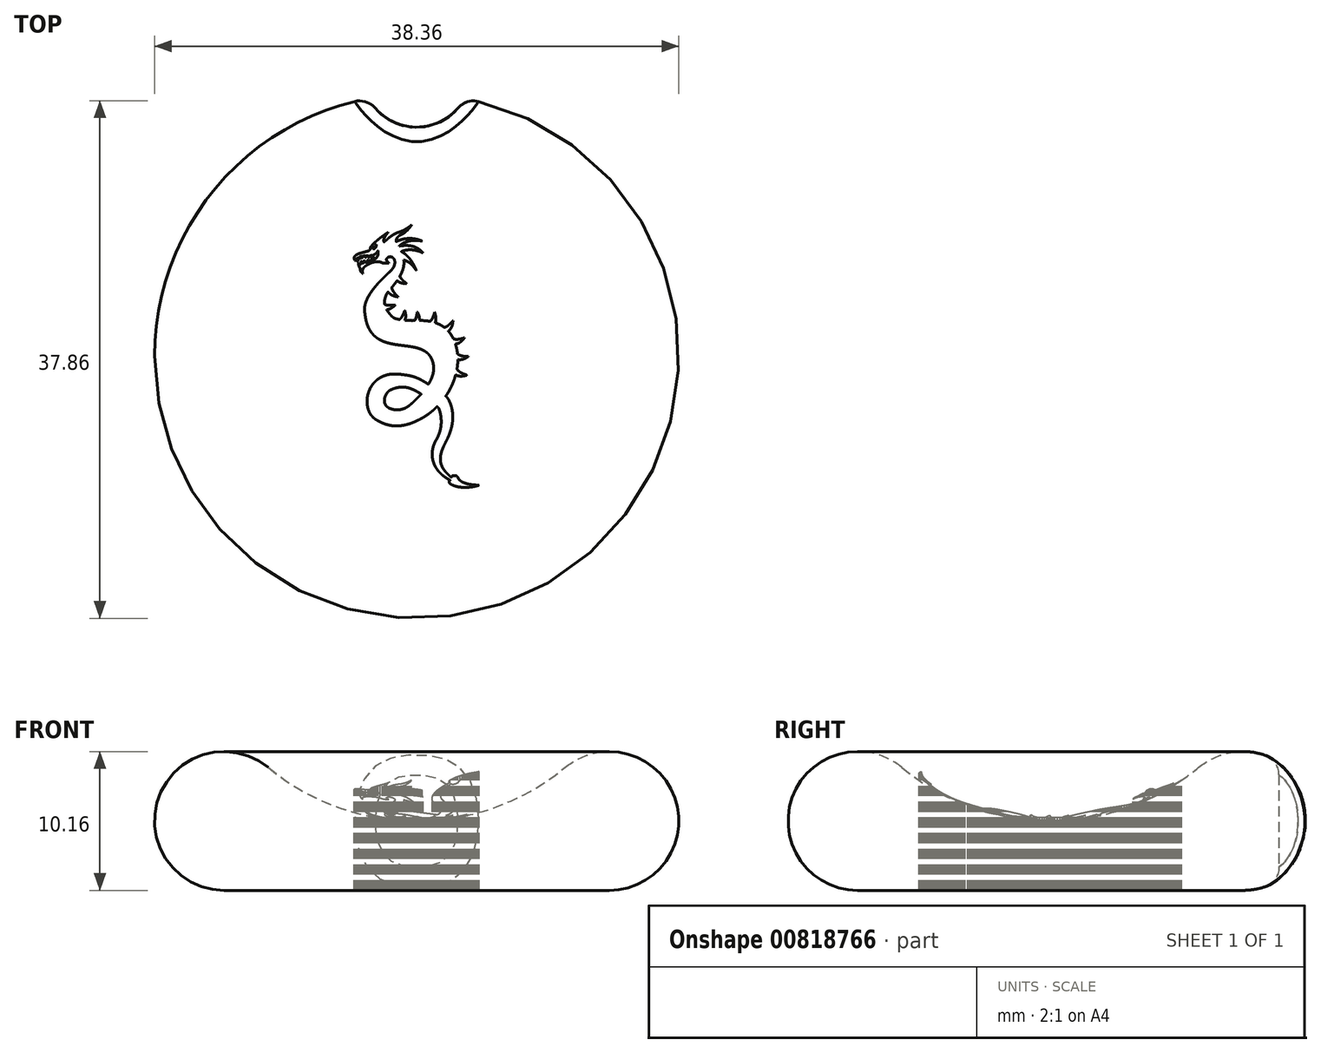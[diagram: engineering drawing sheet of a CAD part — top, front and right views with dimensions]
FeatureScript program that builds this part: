
annotation { "Feature Type Name" : "Feature", "Feature Type Description" : "" }
export const myFeature = defineFeature(function(context is Context, id is Id, definition is map)
    precondition{}
    {
        {
            var Q0;
            Q0=qCreatedBy(makeId("Front.planeOp"),FACE);
            var sketch = newSketch(context, id + "F0", { "sketchPlane" : qUnion([Q0])});
            skArc(sketch, "E0", {"start": v(-10.86, 9) * mm, "mid": v(-18.88, 6.8) * mm, "end": v(-14.1, 0) * mm});
            skArc(sketch, "E1", {"start": v(-10.86, 9) * mm, "mid": v(-5.77, 6.09) * mm, "end": v(0, 5.08) * mm});
            skLineSegment(sketch, "E2", {"start": v(-14.1, 0) * mm, "end": v(0, 0) * mm});
            skLineSegment(sketch, "E3", {"start": v(0, 0) * mm, "end": v(0, 5.08) * mm});
            skPoint(sketch, "E4.orphan", {"position": v(-9.13, 0) * mm});
            skSolve(sketch);
        }
        {
            var Q0;
            Q0=makeQuery(id+"F0.imprint","IMPRINT",FACE,{"disambiguationData":[TD([[makeQuery(id+"F0.imprint","IMPRINT",EDGE,{"derivedFrom":sQuery(id+"F0.wireOp",EDGE,"E0")}),1.0]])]});
            var Q1;
            Q1=sQuery(id+"F0.wireOp",EDGE,"E3");
            revolve(context, id + "F1", {"surfaceOperationType" : NewSurfaceOperationType.NEW, "entities" : qUnion([Q0]), "axis" : qUnion([Q1]), "revolveType" : RevolveType.FULL});
        }
        {
            var Q0;
            Q0=qCreatedBy(makeId("Top.planeOp"),FACE);
            cPlane(context, id + "F2", {"entities" : qUnion([Q0]), "cplaneType" : CPlaneType.OFFSET, "offset" : 10.16 * mm, "width" : 152.4 * mm, "height" : 152.4 * mm});
        }
        {
            var Q0;
            Q0=qCreatedBy(id+"F2.planeOp",FACE);
            var sketch = newSketch(context, id + "F3", { "sketchPlane" : qUnion([Q0])});
            skLineSegment(sketch, "E5", {"start": v(-2.95, 8.17) * mm, "end": v(-2.96, 8.11) * mm});
            skLineSegment(sketch, "E6", {"start": v(-2.96, 8.11) * mm, "end": v(-2.97, 8.05) * mm});
            skLineSegment(sketch, "E7", {"start": v(-2.97, 8.05) * mm, "end": v(-2.98, 8) * mm});
            skLineSegment(sketch, "E8", {"start": v(-2.98, 8) * mm, "end": v(-3, 7.95) * mm});
            skLineSegment(sketch, "E9", {"start": v(-3, 7.95) * mm, "end": v(-3.03, 7.91) * mm});
            skLineSegment(sketch, "E10", {"start": v(-3.03, 7.91) * mm, "end": v(-3.06, 7.88) * mm});
            skLineSegment(sketch, "E11", {"start": v(-3.06, 7.88) * mm, "end": v(-3.09, 7.86) * mm});
            skLineSegment(sketch, "E12", {"start": v(-3.09, 7.86) * mm, "end": v(-3.12, 7.85) * mm});
            skLineSegment(sketch, "E13", {"start": v(-3.12, 7.85) * mm, "end": v(-3.14, 7.85) * mm});
            skLineSegment(sketch, "E14", {"start": v(-3.14, 7.85) * mm, "end": v(-3.16, 7.85) * mm});
            skLineSegment(sketch, "E15", {"start": v(-3.16, 7.85) * mm, "end": v(-3.18, 7.86) * mm});
            skLineSegment(sketch, "E16", {"start": v(-3.18, 7.86) * mm, "end": v(-3.2, 7.88) * mm});
            skLineSegment(sketch, "E17", {"start": v(-3.2, 7.88) * mm, "end": v(-3.2, 7.9) * mm});
            skLineSegment(sketch, "E18", {"start": v(-3.2, 7.9) * mm, "end": v(-3.2, 7.91) * mm});
            skLineSegment(sketch, "E19", {"start": v(-3.2, 7.91) * mm, "end": v(-3.2, 7.93) * mm});
            skLineSegment(sketch, "E20", {"start": v(-3.2, 7.93) * mm, "end": v(-3.17, 7.95) * mm});
            skLineSegment(sketch, "E21", {"start": v(-3.17, 7.95) * mm, "end": v(-3.12, 7.98) * mm});
            skLineSegment(sketch, "E22", {"start": v(-3.12, 7.98) * mm, "end": v(-3.09, 8) * mm});
            skLineSegment(sketch, "E23", {"start": v(-3.09, 8) * mm, "end": v(-3.06, 8.02) * mm});
            skLineSegment(sketch, "E24", {"start": v(-3.06, 8.02) * mm, "end": v(-3.03, 8.05) * mm});
            skLineSegment(sketch, "E25", {"start": v(-3.03, 8.05) * mm, "end": v(-3, 8.09) * mm});
            skLineSegment(sketch, "E26", {"start": v(-3, 8.09) * mm, "end": v(-2.97, 8.13) * mm});
            skLineSegment(sketch, "E27", {"start": v(-2.97, 8.13) * mm, "end": v(-2.95, 8.17) * mm});
            skLineSegment(sketch, "E28", {"start": v(-1.09, -2.26) * mm, "end": v(-1.02, -2.26) * mm});
            skLineSegment(sketch, "E29", {"start": v(-1.02, -2.26) * mm, "end": v(-0.94, -2.26) * mm});
            skLineSegment(sketch, "E30", {"start": v(-0.94, -2.26) * mm, "end": v(-0.87, -2.27) * mm});
            skLineSegment(sketch, "E31", {"start": v(-0.87, -2.27) * mm, "end": v(-0.8, -2.28) * mm});
            skLineSegment(sketch, "E32", {"start": v(-0.8, -2.28) * mm, "end": v(-0.73, -2.3) * mm});
            skLineSegment(sketch, "E33", {"start": v(-0.73, -2.3) * mm, "end": v(-0.66, -2.3) * mm});
            skLineSegment(sketch, "E34", {"start": v(-0.66, -2.3) * mm, "end": v(-0.52, -2.35) * mm});
            skLineSegment(sketch, "E35", {"start": v(-0.52, -2.35) * mm, "end": v(-0.4, -2.4) * mm});
            skLineSegment(sketch, "E36", {"start": v(-0.4, -2.4) * mm, "end": v(-0.26, -2.45) * mm});
            skLineSegment(sketch, "E37", {"start": v(-0.26, -2.45) * mm, "end": v(-0.13, -2.51) * mm});
            skLineSegment(sketch, "E38", {"start": v(-0.13, -2.51) * mm, "end": v(0, -2.58) * mm});
            skLineSegment(sketch, "E39", {"start": v(0, -2.58) * mm, "end": v(0.17, -2.68) * mm});
            skLineSegment(sketch, "E40", {"start": v(0.17, -2.68) * mm, "end": v(0.34, -2.78) * mm});
            skLineSegment(sketch, "E41", {"start": v(0.34, -2.78) * mm, "end": v(0.25, -2.87) * mm});
            skLineSegment(sketch, "E42", {"start": v(0.25, -2.87) * mm, "end": v(0.17, -2.96) * mm});
            skLineSegment(sketch, "E43", {"start": v(0.17, -2.96) * mm, "end": v(0, -3.12) * mm});
            skLineSegment(sketch, "E44", {"start": v(0, -3.12) * mm, "end": v(-0.17, -3.28) * mm});
            skLineSegment(sketch, "E45", {"start": v(-0.17, -3.28) * mm, "end": v(-0.31, -3.42) * mm});
            skLineSegment(sketch, "E46", {"start": v(-0.31, -3.42) * mm, "end": v(-0.4, -3.5) * mm});
            skLineSegment(sketch, "E47", {"start": v(-0.4, -3.5) * mm, "end": v(-0.49, -3.57) * mm});
            skLineSegment(sketch, "E48", {"start": v(-0.49, -3.57) * mm, "end": v(-0.57, -3.64) * mm});
            skLineSegment(sketch, "E49", {"start": v(-0.57, -3.64) * mm, "end": v(-0.66, -3.7) * mm});
            skLineSegment(sketch, "E50", {"start": v(-0.66, -3.7) * mm, "end": v(-0.74, -3.75) * mm});
            skLineSegment(sketch, "E51", {"start": v(-0.74, -3.75) * mm, "end": v(-0.83, -3.8) * mm});
            skLineSegment(sketch, "E52", {"start": v(-0.83, -3.8) * mm, "end": v(-0.91, -3.83) * mm});
            skLineSegment(sketch, "E53", {"start": v(-0.91, -3.83) * mm, "end": v(-1, -3.86) * mm});
            skLineSegment(sketch, "E54", {"start": v(-1, -3.86) * mm, "end": v(-1.09, -3.89) * mm});
            skLineSegment(sketch, "E55", {"start": v(-1.09, -3.89) * mm, "end": v(-1.17, -3.9) * mm});
            skLineSegment(sketch, "E56", {"start": v(-1.17, -3.9) * mm, "end": v(-1.26, -3.92) * mm});
            skLineSegment(sketch, "E57", {"start": v(-1.26, -3.92) * mm, "end": v(-1.35, -3.93) * mm});
            skLineSegment(sketch, "E58", {"start": v(-1.35, -3.93) * mm, "end": v(-1.44, -3.93) * mm});
            skLineSegment(sketch, "E59", {"start": v(-1.44, -3.93) * mm, "end": v(-1.54, -3.92) * mm});
            skLineSegment(sketch, "E60", {"start": v(-1.54, -3.92) * mm, "end": v(-1.63, -3.91) * mm});
            skLineSegment(sketch, "E61", {"start": v(-1.63, -3.91) * mm, "end": v(-1.73, -3.9) * mm});
            skLineSegment(sketch, "E62", {"start": v(-1.73, -3.9) * mm, "end": v(-1.82, -3.88) * mm});
            skLineSegment(sketch, "E63", {"start": v(-1.82, -3.88) * mm, "end": v(-1.9, -3.85) * mm});
            skLineSegment(sketch, "E64", {"start": v(-1.9, -3.85) * mm, "end": v(-1.97, -3.82) * mm});
            skLineSegment(sketch, "E65", {"start": v(-1.97, -3.82) * mm, "end": v(-2.04, -3.79) * mm});
            skLineSegment(sketch, "E66", {"start": v(-2.04, -3.79) * mm, "end": v(-2.1, -3.75) * mm});
            skLineSegment(sketch, "E67", {"start": v(-2.1, -3.75) * mm, "end": v(-2.15, -3.71) * mm});
            skLineSegment(sketch, "E68", {"start": v(-2.15, -3.71) * mm, "end": v(-2.2, -3.67) * mm});
            skLineSegment(sketch, "E69", {"start": v(-2.2, -3.67) * mm, "end": v(-2.24, -3.62) * mm});
            skLineSegment(sketch, "E70", {"start": v(-2.24, -3.62) * mm, "end": v(-2.27, -3.57) * mm});
            skLineSegment(sketch, "E71", {"start": v(-2.27, -3.57) * mm, "end": v(-2.3, -3.52) * mm});
            skLineSegment(sketch, "E72", {"start": v(-2.3, -3.52) * mm, "end": v(-2.32, -3.47) * mm});
            skLineSegment(sketch, "E73", {"start": v(-2.32, -3.47) * mm, "end": v(-2.34, -3.42) * mm});
            skLineSegment(sketch, "E74", {"start": v(-2.34, -3.42) * mm, "end": v(-2.35, -3.36) * mm});
            skLineSegment(sketch, "E75", {"start": v(-2.35, -3.36) * mm, "end": v(-2.36, -3.3) * mm});
            skLineSegment(sketch, "E76", {"start": v(-2.36, -3.3) * mm, "end": v(-2.36, -3.25) * mm});
            skLineSegment(sketch, "E77", {"start": v(-2.36, -3.25) * mm, "end": v(-2.36, -3.2) * mm});
            skLineSegment(sketch, "E78", {"start": v(-2.36, -3.2) * mm, "end": v(-2.35, -3.13) * mm});
            skLineSegment(sketch, "E79", {"start": v(-2.35, -3.13) * mm, "end": v(-2.34, -3.08) * mm});
            skLineSegment(sketch, "E80", {"start": v(-2.34, -3.08) * mm, "end": v(-2.33, -3.02) * mm});
            skLineSegment(sketch, "E81", {"start": v(-2.33, -3.02) * mm, "end": v(-2.31, -2.97) * mm});
            skLineSegment(sketch, "E82", {"start": v(-2.31, -2.97) * mm, "end": v(-2.3, -2.91) * mm});
            skLineSegment(sketch, "E83", {"start": v(-2.3, -2.91) * mm, "end": v(-2.27, -2.86) * mm});
            skLineSegment(sketch, "E84", {"start": v(-2.27, -2.86) * mm, "end": v(-2.24, -2.8) * mm});
            skLineSegment(sketch, "E85", {"start": v(-2.24, -2.8) * mm, "end": v(-2.21, -2.76) * mm});
            skLineSegment(sketch, "E86", {"start": v(-2.21, -2.76) * mm, "end": v(-2.18, -2.71) * mm});
            skLineSegment(sketch, "E87", {"start": v(-2.18, -2.71) * mm, "end": v(-2.15, -2.67) * mm});
            skLineSegment(sketch, "E88", {"start": v(-2.15, -2.67) * mm, "end": v(-2.11, -2.63) * mm});
            skLineSegment(sketch, "E89", {"start": v(-2.11, -2.63) * mm, "end": v(-2.08, -2.6) * mm});
            skLineSegment(sketch, "E90", {"start": v(-2.08, -2.6) * mm, "end": v(-2.04, -2.56) * mm});
            skLineSegment(sketch, "E91", {"start": v(-2.04, -2.56) * mm, "end": v(-2, -2.53) * mm});
            skLineSegment(sketch, "E92", {"start": v(-2, -2.53) * mm, "end": v(-1.96, -2.5) * mm});
            skLineSegment(sketch, "E93", {"start": v(-1.96, -2.5) * mm, "end": v(-1.92, -2.48) * mm});
            skLineSegment(sketch, "E94", {"start": v(-1.92, -2.48) * mm, "end": v(-1.84, -2.44) * mm});
            skLineSegment(sketch, "E95", {"start": v(-1.84, -2.44) * mm, "end": v(-1.76, -2.4) * mm});
            skLineSegment(sketch, "E96", {"start": v(-1.76, -2.4) * mm, "end": v(-1.67, -2.37) * mm});
            skLineSegment(sketch, "E97", {"start": v(-1.67, -2.37) * mm, "end": v(-1.56, -2.34) * mm});
            skLineSegment(sketch, "E98", {"start": v(-1.56, -2.34) * mm, "end": v(-1.46, -2.3) * mm});
            skLineSegment(sketch, "E99", {"start": v(-1.46, -2.3) * mm, "end": v(-1.34, -2.29) * mm});
            skLineSegment(sketch, "E100", {"start": v(-1.34, -2.29) * mm, "end": v(-1.22, -2.27) * mm});
            skLineSegment(sketch, "E101", {"start": v(-1.22, -2.27) * mm, "end": v(-1.09, -2.26) * mm});
            skLineSegment(sketch, "E102", {"start": v(-0.37, 9.6) * mm, "end": v(-0.45, 9.54) * mm});
            skLineSegment(sketch, "E103", {"start": v(-0.45, 9.54) * mm, "end": v(-0.54, 9.47) * mm});
            skLineSegment(sketch, "E104", {"start": v(-0.54, 9.47) * mm, "end": v(-0.66, 9.38) * mm});
            skLineSegment(sketch, "E105", {"start": v(-0.66, 9.38) * mm, "end": v(-0.8, 9.3) * mm});
            skLineSegment(sketch, "E106", {"start": v(-0.8, 9.3) * mm, "end": v(-0.88, 9.25) * mm});
            skLineSegment(sketch, "E107", {"start": v(-0.88, 9.25) * mm, "end": v(-0.97, 9.2) * mm});
            skLineSegment(sketch, "E108", {"start": v(-0.97, 9.2) * mm, "end": v(-1.05, 9.16) * mm});
            skLineSegment(sketch, "E109", {"start": v(-1.05, 9.16) * mm, "end": v(-1.14, 9.13) * mm});
            skLineSegment(sketch, "E110", {"start": v(-1.14, 9.13) * mm, "end": v(-1.23, 9.1) * mm});
            skLineSegment(sketch, "E111", {"start": v(-1.23, 9.1) * mm, "end": v(-1.32, 9.07) * mm});
            skLineSegment(sketch, "E112", {"start": v(-1.32, 9.07) * mm, "end": v(-1.41, 9.04) * mm});
            skLineSegment(sketch, "E113", {"start": v(-1.41, 9.04) * mm, "end": v(-1.5, 9) * mm});
            skLineSegment(sketch, "E114", {"start": v(-1.5, 9) * mm, "end": v(-1.6, 8.95) * mm});
            skLineSegment(sketch, "E115", {"start": v(-1.6, 8.95) * mm, "end": v(-1.69, 8.9) * mm});
            skLineSegment(sketch, "E116", {"start": v(-1.69, 8.9) * mm, "end": v(-1.78, 8.84) * mm});
            skLineSegment(sketch, "E117", {"start": v(-1.78, 8.84) * mm, "end": v(-1.87, 8.78) * mm});
            skLineSegment(sketch, "E118", {"start": v(-1.87, 8.78) * mm, "end": v(-1.95, 8.72) * mm});
            skLineSegment(sketch, "E119", {"start": v(-1.95, 8.72) * mm, "end": v(-2.03, 8.66) * mm});
            skLineSegment(sketch, "E120", {"start": v(-2.03, 8.66) * mm, "end": v(-2.16, 8.54) * mm});
            skLineSegment(sketch, "E121", {"start": v(-2.16, 8.54) * mm, "end": v(-2.27, 8.44) * mm});
            skLineSegment(sketch, "E122", {"start": v(-2.27, 8.44) * mm, "end": v(-2.37, 8.35) * mm});
            skLineSegment(sketch, "E123", {"start": v(-2.37, 8.35) * mm, "end": v(-2.39, 8.37) * mm});
            skLineSegment(sketch, "E124", {"start": v(-2.39, 8.37) * mm, "end": v(-2.4, 8.4) * mm});
            skLineSegment(sketch, "E125", {"start": v(-2.4, 8.4) * mm, "end": v(-2.4, 8.42) * mm});
            skLineSegment(sketch, "E126", {"start": v(-2.4, 8.42) * mm, "end": v(-2.4, 8.45) * mm});
            skLineSegment(sketch, "E127", {"start": v(-2.4, 8.45) * mm, "end": v(-2.4, 8.48) * mm});
            skLineSegment(sketch, "E128", {"start": v(-2.4, 8.48) * mm, "end": v(-2.4, 8.52) * mm});
            skLineSegment(sketch, "E129", {"start": v(-2.4, 8.52) * mm, "end": v(-2.4, 8.56) * mm});
            skLineSegment(sketch, "E130", {"start": v(-2.4, 8.56) * mm, "end": v(-2.39, 8.6) * mm});
            skLineSegment(sketch, "E131", {"start": v(-2.39, 8.6) * mm, "end": v(-2.37, 8.64) * mm});
            skLineSegment(sketch, "E132", {"start": v(-2.37, 8.64) * mm, "end": v(-2.35, 8.69) * mm});
            skLineSegment(sketch, "E133", {"start": v(-2.35, 8.69) * mm, "end": v(-2.33, 8.74) * mm});
            skLineSegment(sketch, "E134", {"start": v(-2.33, 8.74) * mm, "end": v(-2.3, 8.8) * mm});
            skLineSegment(sketch, "E135", {"start": v(-2.3, 8.8) * mm, "end": v(-2.26, 8.85) * mm});
            skLineSegment(sketch, "E136", {"start": v(-2.26, 8.85) * mm, "end": v(-2.21, 8.91) * mm});
            skLineSegment(sketch, "E137", {"start": v(-2.21, 8.91) * mm, "end": v(-2.16, 8.98) * mm});
            skLineSegment(sketch, "E138", {"start": v(-2.16, 8.98) * mm, "end": v(-2.1, 9.05) * mm});
            skLineSegment(sketch, "E139", {"start": v(-2.1, 9.05) * mm, "end": v(-2.33, 8.9) * mm});
            skLineSegment(sketch, "E140", {"start": v(-2.33, 8.9) * mm, "end": v(-2.52, 8.76) * mm});
            skLineSegment(sketch, "E141", {"start": v(-2.52, 8.76) * mm, "end": v(-2.68, 8.64) * mm});
            skLineSegment(sketch, "E142", {"start": v(-2.68, 8.64) * mm, "end": v(-2.82, 8.53) * mm});
            skLineSegment(sketch, "E143", {"start": v(-2.82, 8.53) * mm, "end": v(-2.95, 8.42) * mm});
            skLineSegment(sketch, "E144", {"start": v(-2.95, 8.42) * mm, "end": v(-3.06, 8.32) * mm});
            skLineSegment(sketch, "E145", {"start": v(-3.06, 8.32) * mm, "end": v(-3.18, 8.2) * mm});
            skLineSegment(sketch, "E146", {"start": v(-3.18, 8.2) * mm, "end": v(-3.29, 8.1) * mm});
            skLineSegment(sketch, "E147", {"start": v(-3.29, 8.1) * mm, "end": v(-3.32, 8.06) * mm});
            skLineSegment(sketch, "E148", {"start": v(-3.32, 8.06) * mm, "end": v(-3.34, 8.02) * mm});
            skLineSegment(sketch, "E149", {"start": v(-3.34, 8.02) * mm, "end": v(-3.36, 7.99) * mm});
            skLineSegment(sketch, "E150", {"start": v(-3.36, 7.99) * mm, "end": v(-3.37, 7.95) * mm});
            skLineSegment(sketch, "E151", {"start": v(-3.37, 7.95) * mm, "end": v(-3.39, 7.9) * mm});
            skLineSegment(sketch, "E152", {"start": v(-3.39, 7.9) * mm, "end": v(-3.4, 7.85) * mm});
            skLineSegment(sketch, "E153", {"start": v(-3.4, 7.85) * mm, "end": v(-3.4, 7.82) * mm});
            skLineSegment(sketch, "E154", {"start": v(-3.4, 7.82) * mm, "end": v(-3.4, 7.8) * mm});
            skLineSegment(sketch, "E155", {"start": v(-3.4, 7.8) * mm, "end": v(-3.42, 7.78) * mm});
            skLineSegment(sketch, "E156", {"start": v(-3.42, 7.78) * mm, "end": v(-3.43, 7.76) * mm});
            skLineSegment(sketch, "E157", {"start": v(-3.43, 7.76) * mm, "end": v(-3.45, 7.74) * mm});
            skLineSegment(sketch, "E158", {"start": v(-3.45, 7.74) * mm, "end": v(-3.48, 7.73) * mm});
            skLineSegment(sketch, "E159", {"start": v(-3.48, 7.73) * mm, "end": v(-3.52, 7.7) * mm});
            skLineSegment(sketch, "E160", {"start": v(-3.52, 7.7) * mm, "end": v(-3.57, 7.7) * mm});
            skLineSegment(sketch, "E161", {"start": v(-3.57, 7.7) * mm, "end": v(-3.74, 7.64) * mm});
            skLineSegment(sketch, "E162", {"start": v(-3.74, 7.64) * mm, "end": v(-3.9, 7.6) * mm});
            skLineSegment(sketch, "E163", {"start": v(-3.9, 7.6) * mm, "end": v(-4.04, 7.56) * mm});
            skLineSegment(sketch, "E164", {"start": v(-4.04, 7.56) * mm, "end": v(-4.18, 7.51) * mm});
            skLineSegment(sketch, "E165", {"start": v(-4.18, 7.51) * mm, "end": v(-4.3, 7.47) * mm});
            skLineSegment(sketch, "E166", {"start": v(-4.3, 7.47) * mm, "end": v(-4.36, 7.44) * mm});
            skLineSegment(sketch, "E167", {"start": v(-4.36, 7.44) * mm, "end": v(-4.4, 7.42) * mm});
            skLineSegment(sketch, "E168", {"start": v(-4.4, 7.42) * mm, "end": v(-4.45, 7.4) * mm});
            skLineSegment(sketch, "E169", {"start": v(-4.45, 7.4) * mm, "end": v(-4.48, 7.37) * mm});
            skLineSegment(sketch, "E170", {"start": v(-4.48, 7.37) * mm, "end": v(-4.51, 7.34) * mm});
            skLineSegment(sketch, "E171", {"start": v(-4.51, 7.34) * mm, "end": v(-4.53, 7.31) * mm});
            skLineSegment(sketch, "E172", {"start": v(-4.53, 7.31) * mm, "end": v(-4.55, 7.29) * mm});
            skLineSegment(sketch, "E173", {"start": v(-4.55, 7.29) * mm, "end": v(-4.56, 7.25) * mm});
            skLineSegment(sketch, "E174", {"start": v(-4.56, 7.25) * mm, "end": v(-4.57, 7.22) * mm});
            skLineSegment(sketch, "E175", {"start": v(-4.57, 7.22) * mm, "end": v(-4.57, 7.18) * mm});
            skLineSegment(sketch, "E176", {"start": v(-4.57, 7.18) * mm, "end": v(-4.57, 7.14) * mm});
            skLineSegment(sketch, "E177", {"start": v(-4.57, 7.14) * mm, "end": v(-4.56, 7.1) * mm});
            skLineSegment(sketch, "E178", {"start": v(-4.56, 7.1) * mm, "end": v(-4.54, 7) * mm});
            skLineSegment(sketch, "E179", {"start": v(-4.54, 7) * mm, "end": v(-4.48, 7.06) * mm});
            skLineSegment(sketch, "E180", {"start": v(-4.48, 7.06) * mm, "end": v(-4.45, 7.03) * mm});
            skLineSegment(sketch, "E181", {"start": v(-4.45, 7.03) * mm, "end": v(-4.41, 7) * mm});
            skLineSegment(sketch, "E182", {"start": v(-4.41, 7) * mm, "end": v(-4.37, 6.97) * mm});
            skLineSegment(sketch, "E183", {"start": v(-4.37, 6.97) * mm, "end": v(-4.33, 6.95) * mm});
            skLineSegment(sketch, "E184", {"start": v(-4.33, 6.95) * mm, "end": v(-4.36, 7) * mm});
            skLineSegment(sketch, "E185", {"start": v(-4.36, 7) * mm, "end": v(-4.38, 7.04) * mm});
            skLineSegment(sketch, "E186", {"start": v(-4.38, 7.04) * mm, "end": v(-4.4, 7.08) * mm});
            skLineSegment(sketch, "E187", {"start": v(-4.4, 7.08) * mm, "end": v(-4.4, 7.13) * mm});
            skLineSegment(sketch, "E188", {"start": v(-4.4, 7.13) * mm, "end": v(-4.34, 7.17) * mm});
            skLineSegment(sketch, "E189", {"start": v(-4.34, 7.17) * mm, "end": v(-4.28, 7.2) * mm});
            skLineSegment(sketch, "E190", {"start": v(-4.28, 7.2) * mm, "end": v(-4.27, 7.16) * mm});
            skLineSegment(sketch, "E191", {"start": v(-4.27, 7.16) * mm, "end": v(-4.26, 7.13) * mm});
            skLineSegment(sketch, "E192", {"start": v(-4.26, 7.13) * mm, "end": v(-4.23, 7.1) * mm});
            skLineSegment(sketch, "E193", {"start": v(-4.23, 7.1) * mm, "end": v(-4.2, 7.07) * mm});
            skLineSegment(sketch, "E194", {"start": v(-4.2, 7.07) * mm, "end": v(-4.2, 7.11) * mm});
            skLineSegment(sketch, "E195", {"start": v(-4.2, 7.11) * mm, "end": v(-4.2, 7.16) * mm});
            skLineSegment(sketch, "E196", {"start": v(-4.2, 7.16) * mm, "end": v(-4.2, 7.2) * mm});
            skLineSegment(sketch, "E197", {"start": v(-4.2, 7.2) * mm, "end": v(-4.2, 7.25) * mm});
            skLineSegment(sketch, "E198", {"start": v(-4.2, 7.25) * mm, "end": v(-4.12, 7.28) * mm});
            skLineSegment(sketch, "E199", {"start": v(-4.12, 7.28) * mm, "end": v(-4.04, 7.3) * mm});
            skLineSegment(sketch, "E200", {"start": v(-4.04, 7.3) * mm, "end": v(-4.04, 7.27) * mm});
            skLineSegment(sketch, "E201", {"start": v(-4.04, 7.27) * mm, "end": v(-4.03, 7.23) * mm});
            skLineSegment(sketch, "E202", {"start": v(-4.03, 7.23) * mm, "end": v(-4.02, 7.2) * mm});
            skLineSegment(sketch, "E203", {"start": v(-4.02, 7.2) * mm, "end": v(-4, 7.16) * mm});
            skLineSegment(sketch, "E204", {"start": v(-4, 7.16) * mm, "end": v(-4, 7.2) * mm});
            skLineSegment(sketch, "E205", {"start": v(-4, 7.2) * mm, "end": v(-3.99, 7.24) * mm});
            skLineSegment(sketch, "E206", {"start": v(-3.99, 7.24) * mm, "end": v(-3.97, 7.28) * mm});
            skLineSegment(sketch, "E207", {"start": v(-3.97, 7.28) * mm, "end": v(-3.95, 7.32) * mm});
            skLineSegment(sketch, "E208", {"start": v(-3.95, 7.32) * mm, "end": v(-3.86, 7.33) * mm});
            skLineSegment(sketch, "E209", {"start": v(-3.86, 7.33) * mm, "end": v(-3.78, 7.34) * mm});
            skLineSegment(sketch, "E210", {"start": v(-3.78, 7.34) * mm, "end": v(-3.78, 7.3) * mm});
            skLineSegment(sketch, "E211", {"start": v(-3.78, 7.3) * mm, "end": v(-3.77, 7.27) * mm});
            skLineSegment(sketch, "E212", {"start": v(-3.77, 7.27) * mm, "end": v(-3.76, 7.23) * mm});
            skLineSegment(sketch, "E213", {"start": v(-3.76, 7.23) * mm, "end": v(-3.74, 7.2) * mm});
            skLineSegment(sketch, "E214", {"start": v(-3.74, 7.2) * mm, "end": v(-3.73, 7.24) * mm});
            skLineSegment(sketch, "E215", {"start": v(-3.73, 7.24) * mm, "end": v(-3.73, 7.27) * mm});
            skLineSegment(sketch, "E216", {"start": v(-3.73, 7.27) * mm, "end": v(-3.72, 7.3) * mm});
            skLineSegment(sketch, "E217", {"start": v(-3.72, 7.3) * mm, "end": v(-3.7, 7.34) * mm});
            skLineSegment(sketch, "E218", {"start": v(-3.7, 7.34) * mm, "end": v(-3.55, 7.35) * mm});
            skLineSegment(sketch, "E219", {"start": v(-3.55, 7.35) * mm, "end": v(-3.56, 7.32) * mm});
            skLineSegment(sketch, "E220", {"start": v(-3.56, 7.32) * mm, "end": v(-3.55, 7.3) * mm});
            skLineSegment(sketch, "E221", {"start": v(-3.55, 7.3) * mm, "end": v(-3.55, 7.28) * mm});
            skLineSegment(sketch, "E222", {"start": v(-3.55, 7.28) * mm, "end": v(-3.54, 7.26) * mm});
            skLineSegment(sketch, "E223", {"start": v(-3.54, 7.26) * mm, "end": v(-3.53, 7.24) * mm});
            skLineSegment(sketch, "E224", {"start": v(-3.53, 7.24) * mm, "end": v(-3.51, 7.23) * mm});
            skLineSegment(sketch, "E225", {"start": v(-3.51, 7.23) * mm, "end": v(-3.47, 7.2) * mm});
            skLineSegment(sketch, "E226", {"start": v(-3.47, 7.2) * mm, "end": v(-3.48, 7.23) * mm});
            skLineSegment(sketch, "E227", {"start": v(-3.48, 7.23) * mm, "end": v(-3.49, 7.25) * mm});
            skLineSegment(sketch, "E228", {"start": v(-3.49, 7.25) * mm, "end": v(-3.48, 7.27) * mm});
            skLineSegment(sketch, "E229", {"start": v(-3.48, 7.27) * mm, "end": v(-3.48, 7.3) * mm});
            skLineSegment(sketch, "E230", {"start": v(-3.48, 7.3) * mm, "end": v(-3.47, 7.31) * mm});
            skLineSegment(sketch, "E231", {"start": v(-3.47, 7.31) * mm, "end": v(-3.45, 7.33) * mm});
            skLineSegment(sketch, "E232", {"start": v(-3.45, 7.33) * mm, "end": v(-3.42, 7.35) * mm});
            skLineSegment(sketch, "E233", {"start": v(-3.42, 7.35) * mm, "end": v(-3.34, 7.36) * mm});
            skLineSegment(sketch, "E234", {"start": v(-3.34, 7.36) * mm, "end": v(-3.27, 7.37) * mm});
            skLineSegment(sketch, "E235", {"start": v(-3.27, 7.37) * mm, "end": v(-3.27, 7.34) * mm});
            skLineSegment(sketch, "E236", {"start": v(-3.27, 7.34) * mm, "end": v(-3.27, 7.3) * mm});
            skLineSegment(sketch, "E237", {"start": v(-3.27, 7.3) * mm, "end": v(-3.26, 7.27) * mm});
            skLineSegment(sketch, "E238", {"start": v(-3.26, 7.27) * mm, "end": v(-3.25, 7.26) * mm});
            skLineSegment(sketch, "E239", {"start": v(-3.25, 7.26) * mm, "end": v(-3.23, 7.24) * mm});
            skLineSegment(sketch, "E240", {"start": v(-3.23, 7.24) * mm, "end": v(-3.23, 7.28) * mm});
            skLineSegment(sketch, "E241", {"start": v(-3.23, 7.28) * mm, "end": v(-3.22, 7.32) * mm});
            skLineSegment(sketch, "E242", {"start": v(-3.22, 7.32) * mm, "end": v(-3.2, 7.36) * mm});
            skLineSegment(sketch, "E243", {"start": v(-3.2, 7.36) * mm, "end": v(-3.18, 7.4) * mm});
            skLineSegment(sketch, "E244", {"start": v(-3.18, 7.4) * mm, "end": v(-3.13, 7.42) * mm});
            skLineSegment(sketch, "E245", {"start": v(-3.13, 7.42) * mm, "end": v(-3.08, 7.45) * mm});
            skLineSegment(sketch, "E246", {"start": v(-3.08, 7.45) * mm, "end": v(-3.03, 7.48) * mm});
            skLineSegment(sketch, "E247", {"start": v(-3.03, 7.48) * mm, "end": v(-2.99, 7.52) * mm});
            skLineSegment(sketch, "E248", {"start": v(-2.99, 7.52) * mm, "end": v(-2.94, 7.56) * mm});
            skLineSegment(sketch, "E249", {"start": v(-2.94, 7.56) * mm, "end": v(-2.9, 7.6) * mm});
            skLineSegment(sketch, "E250", {"start": v(-2.9, 7.6) * mm, "end": v(-2.86, 7.66) * mm});
            skLineSegment(sketch, "E251", {"start": v(-2.86, 7.66) * mm, "end": v(-2.82, 7.72) * mm});
            skLineSegment(sketch, "E252", {"start": v(-2.82, 7.72) * mm, "end": v(-2.82, 7.6) * mm});
            skLineSegment(sketch, "E253", {"start": v(-2.82, 7.6) * mm, "end": v(-2.82, 7.51) * mm});
            skLineSegment(sketch, "E254", {"start": v(-2.82, 7.51) * mm, "end": v(-2.83, 7.43) * mm});
            skLineSegment(sketch, "E255", {"start": v(-2.83, 7.43) * mm, "end": v(-2.84, 7.39) * mm});
            skLineSegment(sketch, "E256", {"start": v(-2.84, 7.39) * mm, "end": v(-2.85, 7.35) * mm});
            skLineSegment(sketch, "E257", {"start": v(-2.85, 7.35) * mm, "end": v(-2.87, 7.31) * mm});
            skLineSegment(sketch, "E258", {"start": v(-2.87, 7.31) * mm, "end": v(-2.88, 7.28) * mm});
            skLineSegment(sketch, "E259", {"start": v(-2.88, 7.28) * mm, "end": v(-2.9, 7.25) * mm});
            skLineSegment(sketch, "E260", {"start": v(-2.9, 7.25) * mm, "end": v(-2.93, 7.22) * mm});
            skLineSegment(sketch, "E261", {"start": v(-2.93, 7.22) * mm, "end": v(-2.95, 7.2) * mm});
            skLineSegment(sketch, "E262", {"start": v(-2.95, 7.2) * mm, "end": v(-2.98, 7.16) * mm});
            skLineSegment(sketch, "E263", {"start": v(-2.98, 7.16) * mm, "end": v(-3, 7.14) * mm});
            skLineSegment(sketch, "E264", {"start": v(-3, 7.14) * mm, "end": v(-3.04, 7.12) * mm});
            skLineSegment(sketch, "E265", {"start": v(-3.04, 7.12) * mm, "end": v(-3.06, 7.14) * mm});
            skLineSegment(sketch, "E266", {"start": v(-3.06, 7.14) * mm, "end": v(-3.07, 7.16) * mm});
            skLineSegment(sketch, "E267", {"start": v(-3.07, 7.16) * mm, "end": v(-3.08, 7.19) * mm});
            skLineSegment(sketch, "E268", {"start": v(-3.08, 7.19) * mm, "end": v(-3.09, 7.22) * mm});
            skLineSegment(sketch, "E269", {"start": v(-3.09, 7.22) * mm, "end": v(-3.1, 7.18) * mm});
            skLineSegment(sketch, "E270", {"start": v(-3.1, 7.18) * mm, "end": v(-3.1, 7.15) * mm});
            skLineSegment(sketch, "E271", {"start": v(-3.1, 7.15) * mm, "end": v(-3.1, 7.08) * mm});
            skLineSegment(sketch, "E272", {"start": v(-3.1, 7.08) * mm, "end": v(-3.12, 7.06) * mm});
            skLineSegment(sketch, "E273", {"start": v(-3.12, 7.06) * mm, "end": v(-3.15, 7.05) * mm});
            skLineSegment(sketch, "E274", {"start": v(-3.15, 7.05) * mm, "end": v(-3.2, 7.02) * mm});
            skLineSegment(sketch, "E275", {"start": v(-3.2, 7.02) * mm, "end": v(-3.27, 7) * mm});
            skLineSegment(sketch, "E276", {"start": v(-3.27, 7) * mm, "end": v(-3.28, 7.03) * mm});
            skLineSegment(sketch, "E277", {"start": v(-3.28, 7.03) * mm, "end": v(-3.3, 7.06) * mm});
            skLineSegment(sketch, "E278", {"start": v(-3.3, 7.06) * mm, "end": v(-3.3, 7.1) * mm});
            skLineSegment(sketch, "E279", {"start": v(-3.3, 7.1) * mm, "end": v(-3.29, 7.13) * mm});
            skLineSegment(sketch, "E280", {"start": v(-3.29, 7.13) * mm, "end": v(-3.31, 7.1) * mm});
            skLineSegment(sketch, "E281", {"start": v(-3.31, 7.1) * mm, "end": v(-3.33, 7.05) * mm});
            skLineSegment(sketch, "E282", {"start": v(-3.33, 7.05) * mm, "end": v(-3.34, 7.01) * mm});
            skLineSegment(sketch, "E283", {"start": v(-3.34, 7.01) * mm, "end": v(-3.35, 6.97) * mm});
            skLineSegment(sketch, "E284", {"start": v(-3.35, 6.97) * mm, "end": v(-3.44, 6.94) * mm});
            skLineSegment(sketch, "E285", {"start": v(-3.44, 6.94) * mm, "end": v(-3.53, 6.92) * mm});
            skLineSegment(sketch, "E286", {"start": v(-3.53, 6.92) * mm, "end": v(-3.54, 6.95) * mm});
            skLineSegment(sketch, "E287", {"start": v(-3.54, 6.95) * mm, "end": v(-3.55, 6.98) * mm});
            skLineSegment(sketch, "E288", {"start": v(-3.55, 6.98) * mm, "end": v(-3.55, 7.02) * mm});
            skLineSegment(sketch, "E289", {"start": v(-3.55, 7.02) * mm, "end": v(-3.55, 7.06) * mm});
            skLineSegment(sketch, "E290", {"start": v(-3.55, 7.06) * mm, "end": v(-3.57, 7.02) * mm});
            skLineSegment(sketch, "E291", {"start": v(-3.57, 7.02) * mm, "end": v(-3.6, 6.98) * mm});
            skLineSegment(sketch, "E292", {"start": v(-3.6, 6.98) * mm, "end": v(-3.6, 6.94) * mm});
            skLineSegment(sketch, "E293", {"start": v(-3.6, 6.94) * mm, "end": v(-3.61, 6.9) * mm});
            skLineSegment(sketch, "E294", {"start": v(-3.61, 6.9) * mm, "end": v(-3.77, 6.86) * mm});
            skLineSegment(sketch, "E295", {"start": v(-3.77, 6.86) * mm, "end": v(-3.8, 6.9) * mm});
            skLineSegment(sketch, "E296", {"start": v(-3.8, 6.9) * mm, "end": v(-3.82, 6.93) * mm});
            skLineSegment(sketch, "E297", {"start": v(-3.82, 6.93) * mm, "end": v(-3.83, 6.97) * mm});
            skLineSegment(sketch, "E298", {"start": v(-3.83, 6.97) * mm, "end": v(-3.83, 7.02) * mm});
            skLineSegment(sketch, "E299", {"start": v(-3.83, 7.02) * mm, "end": v(-3.85, 6.96) * mm});
            skLineSegment(sketch, "E300", {"start": v(-3.85, 6.96) * mm, "end": v(-3.86, 6.92) * mm});
            skLineSegment(sketch, "E301", {"start": v(-3.86, 6.92) * mm, "end": v(-3.86, 6.88) * mm});
            skLineSegment(sketch, "E302", {"start": v(-3.86, 6.88) * mm, "end": v(-3.86, 6.84) * mm});
            skLineSegment(sketch, "E303", {"start": v(-3.86, 6.84) * mm, "end": v(-3.92, 6.82) * mm});
            skLineSegment(sketch, "E304", {"start": v(-3.92, 6.82) * mm, "end": v(-3.98, 6.8) * mm});
            skLineSegment(sketch, "E305", {"start": v(-3.98, 6.8) * mm, "end": v(-4, 6.8) * mm});
            skLineSegment(sketch, "E306", {"start": v(-4, 6.8) * mm, "end": v(-4.01, 6.82) * mm});
            skLineSegment(sketch, "E307", {"start": v(-4.01, 6.82) * mm, "end": v(-4.02, 6.84) * mm});
            skLineSegment(sketch, "E308", {"start": v(-4.02, 6.84) * mm, "end": v(-4.03, 6.86) * mm});
            skLineSegment(sketch, "E309", {"start": v(-4.03, 6.86) * mm, "end": v(-4.04, 6.9) * mm});
            skLineSegment(sketch, "E310", {"start": v(-4.04, 6.9) * mm, "end": v(-4.05, 6.94) * mm});
            skLineSegment(sketch, "E311", {"start": v(-4.05, 6.94) * mm, "end": v(-4.07, 6.88) * mm});
            skLineSegment(sketch, "E312", {"start": v(-4.07, 6.88) * mm, "end": v(-4.08, 6.83) * mm});
            skLineSegment(sketch, "E313", {"start": v(-4.08, 6.83) * mm, "end": v(-4.08, 6.78) * mm});
            skLineSegment(sketch, "E314", {"start": v(-4.08, 6.78) * mm, "end": v(-4.08, 6.76) * mm});
            skLineSegment(sketch, "E315", {"start": v(-4.08, 6.76) * mm, "end": v(-4.07, 6.74) * mm});
            skLineSegment(sketch, "E316", {"start": v(-4.07, 6.74) * mm, "end": v(-4.1, 6.72) * mm});
            skLineSegment(sketch, "E317", {"start": v(-4.1, 6.72) * mm, "end": v(-4.13, 6.7) * mm});
            skLineSegment(sketch, "E318", {"start": v(-4.13, 6.7) * mm, "end": v(-4.16, 6.71) * mm});
            skLineSegment(sketch, "E319", {"start": v(-4.16, 6.71) * mm, "end": v(-4.2, 6.73) * mm});
            skLineSegment(sketch, "E320", {"start": v(-4.2, 6.73) * mm, "end": v(-4.21, 6.75) * mm});
            skLineSegment(sketch, "E321", {"start": v(-4.21, 6.75) * mm, "end": v(-4.23, 6.77) * mm});
            skLineSegment(sketch, "E322", {"start": v(-4.23, 6.77) * mm, "end": v(-4.25, 6.79) * mm});
            skLineSegment(sketch, "E323", {"start": v(-4.25, 6.79) * mm, "end": v(-4.27, 6.82) * mm});
            skLineSegment(sketch, "E324", {"start": v(-4.27, 6.82) * mm, "end": v(-4.27, 6.78) * mm});
            skLineSegment(sketch, "E325", {"start": v(-4.27, 6.78) * mm, "end": v(-4.27, 6.75) * mm});
            skLineSegment(sketch, "E326", {"start": v(-4.27, 6.75) * mm, "end": v(-4.27, 6.72) * mm});
            skLineSegment(sketch, "E327", {"start": v(-4.27, 6.72) * mm, "end": v(-4.26, 6.7) * mm});
            skLineSegment(sketch, "E328", {"start": v(-4.26, 6.7) * mm, "end": v(-4.25, 6.67) * mm});
            skLineSegment(sketch, "E329", {"start": v(-4.25, 6.67) * mm, "end": v(-4.24, 6.64) * mm});
            skLineSegment(sketch, "E330", {"start": v(-4.24, 6.64) * mm, "end": v(-4.23, 6.62) * mm});
            skLineSegment(sketch, "E331", {"start": v(-4.23, 6.62) * mm, "end": v(-4.2, 6.6) * mm});
            skLineSegment(sketch, "E332", {"start": v(-4.2, 6.6) * mm, "end": v(-4.23, 6.57) * mm});
            skLineSegment(sketch, "E333", {"start": v(-4.23, 6.57) * mm, "end": v(-4.2, 6.53) * mm});
            skLineSegment(sketch, "E334", {"start": v(-4.2, 6.53) * mm, "end": v(-4.17, 6.5) * mm});
            skLineSegment(sketch, "E335", {"start": v(-4.17, 6.5) * mm, "end": v(-4.15, 6.46) * mm});
            skLineSegment(sketch, "E336", {"start": v(-4.15, 6.46) * mm, "end": v(-4.14, 6.42) * mm});
            skLineSegment(sketch, "E337", {"start": v(-4.14, 6.42) * mm, "end": v(-4.13, 6.35) * mm});
            skLineSegment(sketch, "E338", {"start": v(-4.13, 6.35) * mm, "end": v(-4.12, 6.28) * mm});
            skLineSegment(sketch, "E339", {"start": v(-4.12, 6.28) * mm, "end": v(-4.11, 6.25) * mm});
            skLineSegment(sketch, "E340", {"start": v(-4.11, 6.25) * mm, "end": v(-4.1, 6.22) * mm});
            skLineSegment(sketch, "E341", {"start": v(-4.1, 6.22) * mm, "end": v(-4.1, 6.2) * mm});
            skLineSegment(sketch, "E342", {"start": v(-4.1, 6.2) * mm, "end": v(-4.08, 6.16) * mm});
            skLineSegment(sketch, "E343", {"start": v(-4.08, 6.16) * mm, "end": v(-4.06, 6.13) * mm});
            skLineSegment(sketch, "E344", {"start": v(-4.06, 6.13) * mm, "end": v(-4.03, 6.1) * mm});
            skLineSegment(sketch, "E345", {"start": v(-4.03, 6.1) * mm, "end": v(-4, 6.08) * mm});
            skLineSegment(sketch, "E346", {"start": v(-4, 6.08) * mm, "end": v(-3.95, 6.06) * mm});
            skLineSegment(sketch, "E347", {"start": v(-3.95, 6.06) * mm, "end": v(-3.95, 6.07) * mm});
            skLineSegment(sketch, "E348", {"start": v(-3.95, 6.07) * mm, "end": v(-3.96, 6.1) * mm});
            skLineSegment(sketch, "E349", {"start": v(-3.96, 6.1) * mm, "end": v(-3.97, 6.16) * mm});
            skLineSegment(sketch, "E350", {"start": v(-3.97, 6.16) * mm, "end": v(-3.98, 6.19) * mm});
            skLineSegment(sketch, "E351", {"start": v(-3.98, 6.19) * mm, "end": v(-3.98, 6.22) * mm});
            skLineSegment(sketch, "E352", {"start": v(-3.98, 6.22) * mm, "end": v(-3.97, 6.26) * mm});
            skLineSegment(sketch, "E353", {"start": v(-3.97, 6.26) * mm, "end": v(-3.97, 6.3) * mm});
            skLineSegment(sketch, "E354", {"start": v(-3.97, 6.3) * mm, "end": v(-3.95, 6.34) * mm});
            skLineSegment(sketch, "E355", {"start": v(-3.95, 6.34) * mm, "end": v(-3.93, 6.39) * mm});
            skLineSegment(sketch, "E356", {"start": v(-3.93, 6.39) * mm, "end": v(-3.9, 6.43) * mm});
            skLineSegment(sketch, "E357", {"start": v(-3.9, 6.43) * mm, "end": v(-3.87, 6.48) * mm});
            skLineSegment(sketch, "E358", {"start": v(-3.87, 6.48) * mm, "end": v(-3.83, 6.52) * mm});
            skLineSegment(sketch, "E359", {"start": v(-3.83, 6.52) * mm, "end": v(-3.77, 6.57) * mm});
            skLineSegment(sketch, "E360", {"start": v(-3.77, 6.57) * mm, "end": v(-3.7, 6.62) * mm});
            skLineSegment(sketch, "E361", {"start": v(-3.7, 6.62) * mm, "end": v(-3.64, 6.67) * mm});
            skLineSegment(sketch, "E362", {"start": v(-3.64, 6.67) * mm, "end": v(-3.57, 6.7) * mm});
            skLineSegment(sketch, "E363", {"start": v(-3.57, 6.7) * mm, "end": v(-3.5, 6.75) * mm});
            skLineSegment(sketch, "E364", {"start": v(-3.5, 6.75) * mm, "end": v(-3.41, 6.79) * mm});
            skLineSegment(sketch, "E365", {"start": v(-3.41, 6.79) * mm, "end": v(-3.33, 6.82) * mm});
            skLineSegment(sketch, "E366", {"start": v(-3.33, 6.82) * mm, "end": v(-3.25, 6.85) * mm});
            skLineSegment(sketch, "E367", {"start": v(-3.25, 6.85) * mm, "end": v(-3.17, 6.87) * mm});
            skLineSegment(sketch, "E368", {"start": v(-3.17, 6.87) * mm, "end": v(-3.09, 6.9) * mm});
            skLineSegment(sketch, "E369", {"start": v(-3.09, 6.9) * mm, "end": v(-3, 6.9) * mm});
            skLineSegment(sketch, "E370", {"start": v(-3, 6.9) * mm, "end": v(-2.92, 6.91) * mm});
            skLineSegment(sketch, "E371", {"start": v(-2.92, 6.91) * mm, "end": v(-2.85, 6.92) * mm});
            skLineSegment(sketch, "E372", {"start": v(-2.85, 6.92) * mm, "end": v(-2.77, 6.91) * mm});
            skLineSegment(sketch, "E373", {"start": v(-2.77, 6.91) * mm, "end": v(-2.7, 6.9) * mm});
            skLineSegment(sketch, "E374", {"start": v(-2.7, 6.9) * mm, "end": v(-2.63, 6.88) * mm});
            skLineSegment(sketch, "E375", {"start": v(-2.63, 6.88) * mm, "end": v(-2.57, 6.85) * mm});
            skLineSegment(sketch, "E376", {"start": v(-2.57, 6.85) * mm, "end": v(-2.53, 6.84) * mm});
            skLineSegment(sketch, "E377", {"start": v(-2.53, 6.84) * mm, "end": v(-2.5, 6.82) * mm});
            skLineSegment(sketch, "E378", {"start": v(-2.5, 6.82) * mm, "end": v(-2.44, 6.8) * mm});
            skLineSegment(sketch, "E379", {"start": v(-2.44, 6.8) * mm, "end": v(-2.37, 6.8) * mm});
            skLineSegment(sketch, "E380", {"start": v(-2.37, 6.8) * mm, "end": v(-2.3, 6.8) * mm});
            skLineSegment(sketch, "E381", {"start": v(-2.3, 6.8) * mm, "end": v(-2.23, 6.8) * mm});
            skLineSegment(sketch, "E382", {"start": v(-2.23, 6.8) * mm, "end": v(-2.16, 6.8) * mm});
            skLineSegment(sketch, "E383", {"start": v(-2.16, 6.8) * mm, "end": v(-2.03, 6.82) * mm});
            skLineSegment(sketch, "E384", {"start": v(-2.03, 6.82) * mm, "end": v(-2.1, 6.86) * mm});
            skLineSegment(sketch, "E385", {"start": v(-2.1, 6.86) * mm, "end": v(-2.14, 6.9) * mm});
            skLineSegment(sketch, "E386", {"start": v(-2.14, 6.9) * mm, "end": v(-2.17, 6.94) * mm});
            skLineSegment(sketch, "E387", {"start": v(-2.17, 6.94) * mm, "end": v(-2.2, 6.99) * mm});
            skLineSegment(sketch, "E388", {"start": v(-2.2, 6.99) * mm, "end": v(-2.2, 7.03) * mm});
            skLineSegment(sketch, "E389", {"start": v(-2.2, 7.03) * mm, "end": v(-2.21, 7.07) * mm});
            skLineSegment(sketch, "E390", {"start": v(-2.21, 7.07) * mm, "end": v(-2.2, 7.1) * mm});
            skLineSegment(sketch, "E391", {"start": v(-2.2, 7.1) * mm, "end": v(-2.2, 7.15) * mm});
            skLineSegment(sketch, "E392", {"start": v(-2.2, 7.15) * mm, "end": v(-2.17, 7.18) * mm});
            skLineSegment(sketch, "E393", {"start": v(-2.17, 7.18) * mm, "end": v(-2.14, 7.2) * mm});
            skLineSegment(sketch, "E394", {"start": v(-2.14, 7.2) * mm, "end": v(-2.1, 7.23) * mm});
            skLineSegment(sketch, "E395", {"start": v(-2.1, 7.23) * mm, "end": v(-2.06, 7.25) * mm});
            skLineSegment(sketch, "E396", {"start": v(-2.06, 7.25) * mm, "end": v(-2.02, 7.26) * mm});
            skLineSegment(sketch, "E397", {"start": v(-2.02, 7.26) * mm, "end": v(-1.97, 7.27) * mm});
            skLineSegment(sketch, "E398", {"start": v(-1.97, 7.27) * mm, "end": v(-1.91, 7.27) * mm});
            skLineSegment(sketch, "E399", {"start": v(-1.91, 7.27) * mm, "end": v(-1.85, 7.26) * mm});
            skLineSegment(sketch, "E400", {"start": v(-1.85, 7.26) * mm, "end": v(-1.82, 7.25) * mm});
            skLineSegment(sketch, "E401", {"start": v(-1.82, 7.25) * mm, "end": v(-1.8, 7.24) * mm});
            skLineSegment(sketch, "E402", {"start": v(-1.8, 7.24) * mm, "end": v(-1.77, 7.22) * mm});
            skLineSegment(sketch, "E403", {"start": v(-1.77, 7.22) * mm, "end": v(-1.74, 7.2) * mm});
            skLineSegment(sketch, "E404", {"start": v(-1.74, 7.2) * mm, "end": v(-1.72, 7.2) * mm});
            skLineSegment(sketch, "E405", {"start": v(-1.72, 7.2) * mm, "end": v(-1.7, 7.17) * mm});
            skLineSegment(sketch, "E406", {"start": v(-1.7, 7.17) * mm, "end": v(-1.68, 7.15) * mm});
            skLineSegment(sketch, "E407", {"start": v(-1.68, 7.15) * mm, "end": v(-1.66, 7.12) * mm});
            skLineSegment(sketch, "E408", {"start": v(-1.66, 7.12) * mm, "end": v(-1.64, 7.07) * mm});
            skLineSegment(sketch, "E409", {"start": v(-1.64, 7.07) * mm, "end": v(-1.62, 7) * mm});
            skLineSegment(sketch, "E410", {"start": v(-1.62, 7) * mm, "end": v(-1.6, 6.94) * mm});
            skLineSegment(sketch, "E411", {"start": v(-1.6, 6.94) * mm, "end": v(-1.6, 6.87) * mm});
            skLineSegment(sketch, "E412", {"start": v(-1.6, 6.87) * mm, "end": v(-1.6, 6.8) * mm});
            skLineSegment(sketch, "E413", {"start": v(-1.6, 6.8) * mm, "end": v(-1.62, 6.72) * mm});
            skLineSegment(sketch, "E414", {"start": v(-1.62, 6.72) * mm, "end": v(-1.64, 6.64) * mm});
            skLineSegment(sketch, "E415", {"start": v(-1.64, 6.64) * mm, "end": v(-1.67, 6.56) * mm});
            skLineSegment(sketch, "E416", {"start": v(-1.67, 6.56) * mm, "end": v(-1.7, 6.49) * mm});
            skLineSegment(sketch, "E417", {"start": v(-1.7, 6.49) * mm, "end": v(-1.76, 6.4) * mm});
            skLineSegment(sketch, "E418", {"start": v(-1.76, 6.4) * mm, "end": v(-1.81, 6.33) * mm});
            skLineSegment(sketch, "E419", {"start": v(-1.81, 6.33) * mm, "end": v(-1.88, 6.26) * mm});
            skLineSegment(sketch, "E420", {"start": v(-1.88, 6.26) * mm, "end": v(-2.09, 6.06) * mm});
            skLineSegment(sketch, "E421", {"start": v(-2.09, 6.06) * mm, "end": v(-2.22, 5.93) * mm});
            skLineSegment(sketch, "E422", {"start": v(-2.22, 5.93) * mm, "end": v(-2.38, 5.78) * mm});
            skLineSegment(sketch, "E423", {"start": v(-2.38, 5.78) * mm, "end": v(-2.55, 5.61) * mm});
            skLineSegment(sketch, "E424", {"start": v(-2.55, 5.61) * mm, "end": v(-2.73, 5.43) * mm});
            skLineSegment(sketch, "E425", {"start": v(-2.73, 5.43) * mm, "end": v(-2.9, 5.23) * mm});
            skLineSegment(sketch, "E426", {"start": v(-2.9, 5.23) * mm, "end": v(-3, 5.13) * mm});
            skLineSegment(sketch, "E427", {"start": v(-3, 5.13) * mm, "end": v(-3.08, 5.02) * mm});
            skLineSegment(sketch, "E428", {"start": v(-3.08, 5.02) * mm, "end": v(-3.17, 4.91) * mm});
            skLineSegment(sketch, "E429", {"start": v(-3.17, 4.91) * mm, "end": v(-3.25, 4.8) * mm});
            skLineSegment(sketch, "E430", {"start": v(-3.25, 4.8) * mm, "end": v(-3.33, 4.69) * mm});
            skLineSegment(sketch, "E431", {"start": v(-3.33, 4.69) * mm, "end": v(-3.4, 4.57) * mm});
            skLineSegment(sketch, "E432", {"start": v(-3.4, 4.57) * mm, "end": v(-3.48, 4.46) * mm});
            skLineSegment(sketch, "E433", {"start": v(-3.48, 4.46) * mm, "end": v(-3.55, 4.34) * mm});
            skLineSegment(sketch, "E434", {"start": v(-3.55, 4.34) * mm, "end": v(-3.6, 4.22) * mm});
            skLineSegment(sketch, "E435", {"start": v(-3.6, 4.22) * mm, "end": v(-3.66, 4.1) * mm});
            skLineSegment(sketch, "E436", {"start": v(-3.66, 4.1) * mm, "end": v(-3.71, 3.98) * mm});
            skLineSegment(sketch, "E437", {"start": v(-3.71, 3.98) * mm, "end": v(-3.75, 3.86) * mm});
            skLineSegment(sketch, "E438", {"start": v(-3.75, 3.86) * mm, "end": v(-3.78, 3.74) * mm});
            skLineSegment(sketch, "E439", {"start": v(-3.78, 3.74) * mm, "end": v(-3.8, 3.62) * mm});
            skLineSegment(sketch, "E440", {"start": v(-3.8, 3.62) * mm, "end": v(-3.82, 3.5) * mm});
            skLineSegment(sketch, "E441", {"start": v(-3.82, 3.5) * mm, "end": v(-3.82, 3.44) * mm});
            skLineSegment(sketch, "E442", {"start": v(-3.82, 3.44) * mm, "end": v(-3.82, 3.38) * mm});
            skLineSegment(sketch, "E443", {"start": v(-3.82, 3.38) * mm, "end": v(-3.82, 3.32) * mm});
            skLineSegment(sketch, "E444", {"start": v(-3.82, 3.32) * mm, "end": v(-3.81, 3.26) * mm});
            skLineSegment(sketch, "E445", {"start": v(-3.81, 3.26) * mm, "end": v(-3.8, 3.2) * mm});
            skLineSegment(sketch, "E446", {"start": v(-3.8, 3.2) * mm, "end": v(-3.8, 3.14) * mm});
            skLineSegment(sketch, "E447", {"start": v(-3.8, 3.14) * mm, "end": v(-3.77, 2.97) * mm});
            skLineSegment(sketch, "E448", {"start": v(-3.77, 2.97) * mm, "end": v(-3.75, 2.81) * mm});
            skLineSegment(sketch, "E449", {"start": v(-3.75, 2.81) * mm, "end": v(-3.72, 2.66) * mm});
            skLineSegment(sketch, "E450", {"start": v(-3.72, 2.66) * mm, "end": v(-3.68, 2.52) * mm});
            skLineSegment(sketch, "E451", {"start": v(-3.68, 2.52) * mm, "end": v(-3.64, 2.38) * mm});
            skLineSegment(sketch, "E452", {"start": v(-3.64, 2.38) * mm, "end": v(-3.6, 2.25) * mm});
            skLineSegment(sketch, "E453", {"start": v(-3.6, 2.25) * mm, "end": v(-3.55, 2.13) * mm});
            skLineSegment(sketch, "E454", {"start": v(-3.55, 2.13) * mm, "end": v(-3.5, 2.02) * mm});
            skLineSegment(sketch, "E455", {"start": v(-3.5, 2.02) * mm, "end": v(-3.44, 1.92) * mm});
            skLineSegment(sketch, "E456", {"start": v(-3.44, 1.92) * mm, "end": v(-3.37, 1.82) * mm});
            skLineSegment(sketch, "E457", {"start": v(-3.37, 1.82) * mm, "end": v(-3.3, 1.72) * mm});
            skLineSegment(sketch, "E458", {"start": v(-3.3, 1.72) * mm, "end": v(-3.24, 1.64) * mm});
            skLineSegment(sketch, "E459", {"start": v(-3.24, 1.64) * mm, "end": v(-3.17, 1.56) * mm});
            skLineSegment(sketch, "E460", {"start": v(-3.17, 1.56) * mm, "end": v(-3.1, 1.48) * mm});
            skLineSegment(sketch, "E461", {"start": v(-3.1, 1.48) * mm, "end": v(-3.01, 1.41) * mm});
            skLineSegment(sketch, "E462", {"start": v(-3.01, 1.41) * mm, "end": v(-2.93, 1.35) * mm});
            skLineSegment(sketch, "E463", {"start": v(-2.93, 1.35) * mm, "end": v(-2.85, 1.29) * mm});
            skLineSegment(sketch, "E464", {"start": v(-2.85, 1.29) * mm, "end": v(-2.76, 1.23) * mm});
            skLineSegment(sketch, "E465", {"start": v(-2.76, 1.23) * mm, "end": v(-2.67, 1.18) * mm});
            skLineSegment(sketch, "E466", {"start": v(-2.67, 1.18) * mm, "end": v(-2.58, 1.14) * mm});
            skLineSegment(sketch, "E467", {"start": v(-2.58, 1.14) * mm, "end": v(-2.48, 1.1) * mm});
            skLineSegment(sketch, "E468", {"start": v(-2.48, 1.1) * mm, "end": v(-2.39, 1.06) * mm});
            skLineSegment(sketch, "E469", {"start": v(-2.39, 1.06) * mm, "end": v(-2.29, 1.02) * mm});
            skLineSegment(sketch, "E470", {"start": v(-2.29, 1.02) * mm, "end": v(-2.19, 1) * mm});
            skLineSegment(sketch, "E471", {"start": v(-2.19, 1) * mm, "end": v(-2.09, 0.96) * mm});
            skLineSegment(sketch, "E472", {"start": v(-2.09, 0.96) * mm, "end": v(-1.98, 0.94) * mm});
            skLineSegment(sketch, "E473", {"start": v(-1.98, 0.94) * mm, "end": v(-1.78, 0.9) * mm});
            skLineSegment(sketch, "E474", {"start": v(-1.78, 0.9) * mm, "end": v(-1.57, 0.85) * mm});
            skLineSegment(sketch, "E475", {"start": v(-1.57, 0.85) * mm, "end": v(-1.35, 0.82) * mm});
            skLineSegment(sketch, "E476", {"start": v(-1.35, 0.82) * mm, "end": v(-0.93, 0.77) * mm});
            skLineSegment(sketch, "E477", {"start": v(-0.93, 0.77) * mm, "end": v(-0.72, 0.74) * mm});
            skLineSegment(sketch, "E478", {"start": v(-0.72, 0.74) * mm, "end": v(-0.5, 0.7) * mm});
            skLineSegment(sketch, "E479", {"start": v(-0.5, 0.7) * mm, "end": v(-0.3, 0.68) * mm});
            skLineSegment(sketch, "E480", {"start": v(-0.3, 0.68) * mm, "end": v(-0.11, 0.64) * mm});
            skLineSegment(sketch, "E481", {"start": v(-0.11, 0.64) * mm, "end": v(-0.02, 0.61) * mm});
            skLineSegment(sketch, "E482", {"start": v(-0.02, 0.61) * mm, "end": v(0.08, 0.59) * mm});
            skLineSegment(sketch, "E483", {"start": v(0.08, 0.59) * mm, "end": v(0.17, 0.56) * mm});
            skLineSegment(sketch, "E484", {"start": v(0.17, 0.56) * mm, "end": v(0.26, 0.53) * mm});
            skLineSegment(sketch, "E485", {"start": v(0.26, 0.53) * mm, "end": v(0.34, 0.5) * mm});
            skLineSegment(sketch, "E486", {"start": v(0.34, 0.5) * mm, "end": v(0.43, 0.46) * mm});
            skLineSegment(sketch, "E487", {"start": v(0.43, 0.46) * mm, "end": v(0.5, 0.42) * mm});
            skLineSegment(sketch, "E488", {"start": v(0.5, 0.42) * mm, "end": v(0.58, 0.37) * mm});
            skLineSegment(sketch, "E489", {"start": v(0.58, 0.37) * mm, "end": v(0.66, 0.32) * mm});
            skLineSegment(sketch, "E490", {"start": v(0.66, 0.32) * mm, "end": v(0.73, 0.27) * mm});
            skLineSegment(sketch, "E491", {"start": v(0.73, 0.27) * mm, "end": v(0.8, 0.21) * mm});
            skLineSegment(sketch, "E492", {"start": v(0.8, 0.21) * mm, "end": v(0.86, 0.15) * mm});
            skLineSegment(sketch, "E493", {"start": v(0.86, 0.15) * mm, "end": v(0.92, 0.08) * mm});
            skLineSegment(sketch, "E494", {"start": v(0.92, 0.08) * mm, "end": v(0.97, 0) * mm});
            skLineSegment(sketch, "E495", {"start": v(0.97, 0) * mm, "end": v(1.02, -0.07) * mm});
            skLineSegment(sketch, "E496", {"start": v(1.02, -0.07) * mm, "end": v(1.07, -0.15) * mm});
            skLineSegment(sketch, "E497", {"start": v(1.07, -0.15) * mm, "end": v(1.11, -0.25) * mm});
            skLineSegment(sketch, "E498", {"start": v(1.11, -0.25) * mm, "end": v(1.15, -0.34) * mm});
            skLineSegment(sketch, "E499", {"start": v(1.15, -0.34) * mm, "end": v(1.18, -0.45) * mm});
            skLineSegment(sketch, "E500", {"start": v(1.18, -0.45) * mm, "end": v(1.21, -0.56) * mm});
            skLineSegment(sketch, "E501", {"start": v(1.21, -0.56) * mm, "end": v(1.23, -0.65) * mm});
            skLineSegment(sketch, "E502", {"start": v(1.23, -0.65) * mm, "end": v(1.24, -0.75) * mm});
            skLineSegment(sketch, "E503", {"start": v(1.24, -0.75) * mm, "end": v(1.25, -0.85) * mm});
            skLineSegment(sketch, "E504", {"start": v(1.25, -0.85) * mm, "end": v(1.24, -0.95) * mm});
            skLineSegment(sketch, "E505", {"start": v(1.24, -0.95) * mm, "end": v(1.24, -1.04) * mm});
            skLineSegment(sketch, "E506", {"start": v(1.24, -1.04) * mm, "end": v(1.23, -1.14) * mm});
            skLineSegment(sketch, "E507", {"start": v(1.23, -1.14) * mm, "end": v(1.2, -1.24) * mm});
            skLineSegment(sketch, "E508", {"start": v(1.2, -1.24) * mm, "end": v(1.18, -1.33) * mm});
            skLineSegment(sketch, "E509", {"start": v(1.18, -1.33) * mm, "end": v(1.16, -1.43) * mm});
            skLineSegment(sketch, "E510", {"start": v(1.16, -1.43) * mm, "end": v(1.13, -1.52) * mm});
            skLineSegment(sketch, "E511", {"start": v(1.13, -1.52) * mm, "end": v(1.09, -1.61) * mm});
            skLineSegment(sketch, "E512", {"start": v(1.09, -1.61) * mm, "end": v(1.05, -1.7) * mm});
            skLineSegment(sketch, "E513", {"start": v(1.05, -1.7) * mm, "end": v(1, -1.8) * mm});
            skLineSegment(sketch, "E514", {"start": v(1, -1.8) * mm, "end": v(0.96, -1.89) * mm});
            skLineSegment(sketch, "E515", {"start": v(0.96, -1.89) * mm, "end": v(0.9, -1.98) * mm});
            skLineSegment(sketch, "E516", {"start": v(0.9, -1.98) * mm, "end": v(0.86, -2.06) * mm});
            skLineSegment(sketch, "E517", {"start": v(0.86, -2.06) * mm, "end": v(0.77, -2) * mm});
            skLineSegment(sketch, "E518", {"start": v(0.77, -2) * mm, "end": v(0.68, -1.94) * mm});
            skLineSegment(sketch, "E519", {"start": v(0.68, -1.94) * mm, "end": v(0.5, -1.83) * mm});
            skLineSegment(sketch, "E520", {"start": v(0.5, -1.83) * mm, "end": v(0.37, -1.77) * mm});
            skLineSegment(sketch, "E521", {"start": v(0.37, -1.77) * mm, "end": v(0.26, -1.7) * mm});
            skLineSegment(sketch, "E522", {"start": v(0.26, -1.7) * mm, "end": v(0.15, -1.65) * mm});
            skLineSegment(sketch, "E523", {"start": v(0.15, -1.65) * mm, "end": v(0.05, -1.6) * mm});
            skLineSegment(sketch, "E524", {"start": v(0.05, -1.6) * mm, "end": v(-0.05, -1.57) * mm});
            skLineSegment(sketch, "E525", {"start": v(-0.05, -1.57) * mm, "end": v(-0.15, -1.53) * mm});
            skLineSegment(sketch, "E526", {"start": v(-0.15, -1.53) * mm, "end": v(-0.25, -1.5) * mm});
            skLineSegment(sketch, "E527", {"start": v(-0.25, -1.5) * mm, "end": v(-0.34, -1.47) * mm});
            skLineSegment(sketch, "E528", {"start": v(-0.34, -1.47) * mm, "end": v(-0.44, -1.44) * mm});
            skLineSegment(sketch, "E529", {"start": v(-0.44, -1.44) * mm, "end": v(-0.54, -1.42) * mm});
            skLineSegment(sketch, "E530", {"start": v(-0.54, -1.42) * mm, "end": v(-0.76, -1.39) * mm});
            skLineSegment(sketch, "E531", {"start": v(-0.76, -1.39) * mm, "end": v(-1, -1.35) * mm});
            skLineSegment(sketch, "E532", {"start": v(-1, -1.35) * mm, "end": v(-1.28, -1.32) * mm});
            skLineSegment(sketch, "E533", {"start": v(-1.28, -1.32) * mm, "end": v(-1.4, -1.31) * mm});
            skLineSegment(sketch, "E534", {"start": v(-1.4, -1.31) * mm, "end": v(-1.5, -1.3) * mm});
            skLineSegment(sketch, "E535", {"start": v(-1.5, -1.3) * mm, "end": v(-1.6, -1.3) * mm});
            skLineSegment(sketch, "E536", {"start": v(-1.6, -1.3) * mm, "end": v(-1.71, -1.3) * mm});
            skLineSegment(sketch, "E537", {"start": v(-1.71, -1.3) * mm, "end": v(-1.82, -1.31) * mm});
            skLineSegment(sketch, "E538", {"start": v(-1.82, -1.31) * mm, "end": v(-1.91, -1.32) * mm});
            skLineSegment(sketch, "E539", {"start": v(-1.91, -1.32) * mm, "end": v(-2, -1.34) * mm});
            skLineSegment(sketch, "E540", {"start": v(-2, -1.34) * mm, "end": v(-2.1, -1.36) * mm});
            skLineSegment(sketch, "E541", {"start": v(-2.1, -1.36) * mm, "end": v(-2.2, -1.38) * mm});
            skLineSegment(sketch, "E542", {"start": v(-2.2, -1.38) * mm, "end": v(-2.28, -1.4) * mm});
            skLineSegment(sketch, "E543", {"start": v(-2.28, -1.4) * mm, "end": v(-2.36, -1.43) * mm});
            skLineSegment(sketch, "E544", {"start": v(-2.36, -1.43) * mm, "end": v(-2.45, -1.46) * mm});
            skLineSegment(sketch, "E545", {"start": v(-2.45, -1.46) * mm, "end": v(-2.53, -1.5) * mm});
            skLineSegment(sketch, "E546", {"start": v(-2.53, -1.5) * mm, "end": v(-2.6, -1.54) * mm});
            skLineSegment(sketch, "E547", {"start": v(-2.6, -1.54) * mm, "end": v(-2.67, -1.58) * mm});
            skLineSegment(sketch, "E548", {"start": v(-2.67, -1.58) * mm, "end": v(-2.75, -1.62) * mm});
            skLineSegment(sketch, "E549", {"start": v(-2.75, -1.62) * mm, "end": v(-2.81, -1.67) * mm});
            skLineSegment(sketch, "E550", {"start": v(-2.81, -1.67) * mm, "end": v(-2.88, -1.72) * mm});
            skLineSegment(sketch, "E551", {"start": v(-2.88, -1.72) * mm, "end": v(-2.94, -1.77) * mm});
            skLineSegment(sketch, "E552", {"start": v(-2.94, -1.77) * mm, "end": v(-3, -1.82) * mm});
            skLineSegment(sketch, "E553", {"start": v(-3, -1.82) * mm, "end": v(-3.06, -1.88) * mm});
            skLineSegment(sketch, "E554", {"start": v(-3.06, -1.88) * mm, "end": v(-3.11, -1.94) * mm});
            skLineSegment(sketch, "E555", {"start": v(-3.11, -1.94) * mm, "end": v(-3.16, -2) * mm});
            skLineSegment(sketch, "E556", {"start": v(-3.16, -2) * mm, "end": v(-3.21, -2.06) * mm});
            skLineSegment(sketch, "E557", {"start": v(-3.21, -2.06) * mm, "end": v(-3.26, -2.12) * mm});
            skLineSegment(sketch, "E558", {"start": v(-3.26, -2.12) * mm, "end": v(-3.3, -2.19) * mm});
            skLineSegment(sketch, "E559", {"start": v(-3.3, -2.19) * mm, "end": v(-3.34, -2.25) * mm});
            skLineSegment(sketch, "E560", {"start": v(-3.34, -2.25) * mm, "end": v(-3.38, -2.32) * mm});
            skLineSegment(sketch, "E561", {"start": v(-3.38, -2.32) * mm, "end": v(-3.42, -2.39) * mm});
            skLineSegment(sketch, "E562", {"start": v(-3.42, -2.39) * mm, "end": v(-3.45, -2.46) * mm});
            skLineSegment(sketch, "E563", {"start": v(-3.45, -2.46) * mm, "end": v(-3.48, -2.53) * mm});
            skLineSegment(sketch, "E564", {"start": v(-3.48, -2.53) * mm, "end": v(-3.5, -2.6) * mm});
            skLineSegment(sketch, "E565", {"start": v(-3.5, -2.6) * mm, "end": v(-3.53, -2.67) * mm});
            skLineSegment(sketch, "E566", {"start": v(-3.53, -2.67) * mm, "end": v(-3.55, -2.75) * mm});
            skLineSegment(sketch, "E567", {"start": v(-3.55, -2.75) * mm, "end": v(-3.57, -2.82) * mm});
            skLineSegment(sketch, "E568", {"start": v(-3.57, -2.82) * mm, "end": v(-3.59, -2.9) * mm});
            skLineSegment(sketch, "E569", {"start": v(-3.59, -2.9) * mm, "end": v(-3.6, -2.97) * mm});
            skLineSegment(sketch, "E570", {"start": v(-3.6, -2.97) * mm, "end": v(-3.61, -3.04) * mm});
            skLineSegment(sketch, "E571", {"start": v(-3.61, -3.04) * mm, "end": v(-3.62, -3.12) * mm});
            skLineSegment(sketch, "E572", {"start": v(-3.62, -3.12) * mm, "end": v(-3.63, -3.2) * mm});
            skLineSegment(sketch, "E573", {"start": v(-3.63, -3.2) * mm, "end": v(-3.63, -3.27) * mm});
            skLineSegment(sketch, "E574", {"start": v(-3.63, -3.27) * mm, "end": v(-3.63, -3.34) * mm});
            skLineSegment(sketch, "E575", {"start": v(-3.63, -3.34) * mm, "end": v(-3.63, -3.42) * mm});
            skLineSegment(sketch, "E576", {"start": v(-3.63, -3.42) * mm, "end": v(-3.63, -3.49) * mm});
            skLineSegment(sketch, "E577", {"start": v(-3.63, -3.49) * mm, "end": v(-3.62, -3.56) * mm});
            skLineSegment(sketch, "E578", {"start": v(-3.62, -3.56) * mm, "end": v(-3.6, -3.63) * mm});
            skLineSegment(sketch, "E579", {"start": v(-3.6, -3.63) * mm, "end": v(-3.6, -3.7) * mm});
            skLineSegment(sketch, "E580", {"start": v(-3.6, -3.7) * mm, "end": v(-3.58, -3.77) * mm});
            skLineSegment(sketch, "E581", {"start": v(-3.58, -3.77) * mm, "end": v(-3.56, -3.84) * mm});
            skLineSegment(sketch, "E582", {"start": v(-3.56, -3.84) * mm, "end": v(-3.54, -3.9) * mm});
            skLineSegment(sketch, "E583", {"start": v(-3.54, -3.9) * mm, "end": v(-3.52, -3.97) * mm});
            skLineSegment(sketch, "E584", {"start": v(-3.52, -3.97) * mm, "end": v(-3.5, -4.04) * mm});
            skLineSegment(sketch, "E585", {"start": v(-3.5, -4.04) * mm, "end": v(-3.46, -4.1) * mm});
            skLineSegment(sketch, "E586", {"start": v(-3.46, -4.1) * mm, "end": v(-3.43, -4.16) * mm});
            skLineSegment(sketch, "E587", {"start": v(-3.43, -4.16) * mm, "end": v(-3.4, -4.22) * mm});
            skLineSegment(sketch, "E588", {"start": v(-3.4, -4.22) * mm, "end": v(-3.36, -4.28) * mm});
            skLineSegment(sketch, "E589", {"start": v(-3.36, -4.28) * mm, "end": v(-3.32, -4.33) * mm});
            skLineSegment(sketch, "E590", {"start": v(-3.32, -4.33) * mm, "end": v(-3.28, -4.39) * mm});
            skLineSegment(sketch, "E591", {"start": v(-3.28, -4.39) * mm, "end": v(-3.24, -4.44) * mm});
            skLineSegment(sketch, "E592", {"start": v(-3.24, -4.44) * mm, "end": v(-3.19, -4.48) * mm});
            skLineSegment(sketch, "E593", {"start": v(-3.19, -4.48) * mm, "end": v(-3.14, -4.53) * mm});
            skLineSegment(sketch, "E594", {"start": v(-3.14, -4.53) * mm, "end": v(-3.09, -4.57) * mm});
            skLineSegment(sketch, "E595", {"start": v(-3.09, -4.57) * mm, "end": v(-3.03, -4.61) * mm});
            skLineSegment(sketch, "E596", {"start": v(-3.03, -4.61) * mm, "end": v(-2.97, -4.65) * mm});
            skLineSegment(sketch, "E597", {"start": v(-2.97, -4.65) * mm, "end": v(-2.82, -4.74) * mm});
            skLineSegment(sketch, "E598", {"start": v(-2.82, -4.74) * mm, "end": v(-2.66, -4.82) * mm});
            skLineSegment(sketch, "E599", {"start": v(-2.66, -4.82) * mm, "end": v(-2.58, -4.86) * mm});
            skLineSegment(sketch, "E600", {"start": v(-2.58, -4.86) * mm, "end": v(-2.5, -4.9) * mm});
            skLineSegment(sketch, "E601", {"start": v(-2.5, -4.9) * mm, "end": v(-2.41, -4.93) * mm});
            skLineSegment(sketch, "E602", {"start": v(-2.41, -4.93) * mm, "end": v(-2.32, -4.96) * mm});
            skLineSegment(sketch, "E603", {"start": v(-2.32, -4.96) * mm, "end": v(-2.23, -5) * mm});
            skLineSegment(sketch, "E604", {"start": v(-2.23, -5) * mm, "end": v(-2.14, -5.02) * mm});
            skLineSegment(sketch, "E605", {"start": v(-2.14, -5.02) * mm, "end": v(-2.05, -5.04) * mm});
            skLineSegment(sketch, "E606", {"start": v(-2.05, -5.04) * mm, "end": v(-1.95, -5.06) * mm});
            skLineSegment(sketch, "E607", {"start": v(-1.95, -5.06) * mm, "end": v(-1.86, -5.08) * mm});
            skLineSegment(sketch, "E608", {"start": v(-1.86, -5.08) * mm, "end": v(-1.75, -5.1) * mm});
            skLineSegment(sketch, "E609", {"start": v(-1.75, -5.1) * mm, "end": v(-1.65, -5.1) * mm});
            skLineSegment(sketch, "E610", {"start": v(-1.65, -5.1) * mm, "end": v(-1.55, -5.1) * mm});
            skLineSegment(sketch, "E611", {"start": v(-1.55, -5.1) * mm, "end": v(-1.44, -5.1) * mm});
            skLineSegment(sketch, "E612", {"start": v(-1.44, -5.1) * mm, "end": v(-1.33, -5.1) * mm});
            skLineSegment(sketch, "E613", {"start": v(-1.33, -5.1) * mm, "end": v(-1.22, -5.1) * mm});
            skLineSegment(sketch, "E614", {"start": v(-1.22, -5.1) * mm, "end": v(-1.1, -5.08) * mm});
            skLineSegment(sketch, "E615", {"start": v(-1.1, -5.08) * mm, "end": v(-0.98, -5.06) * mm});
            skLineSegment(sketch, "E616", {"start": v(-0.98, -5.06) * mm, "end": v(-0.86, -5.04) * mm});
            skLineSegment(sketch, "E617", {"start": v(-0.86, -5.04) * mm, "end": v(-0.74, -5) * mm});
            skLineSegment(sketch, "E618", {"start": v(-0.74, -5) * mm, "end": v(-0.6, -4.97) * mm});
            skLineSegment(sketch, "E619", {"start": v(-0.6, -4.97) * mm, "end": v(-0.48, -4.93) * mm});
            skLineSegment(sketch, "E620", {"start": v(-0.48, -4.93) * mm, "end": v(-0.34, -4.88) * mm});
            skLineSegment(sketch, "E621", {"start": v(-0.34, -4.88) * mm, "end": v(-0.2, -4.83) * mm});
            skLineSegment(sketch, "E622", {"start": v(-0.2, -4.83) * mm, "end": v(-0.07, -4.77) * mm});
            skLineSegment(sketch, "E623", {"start": v(-0.07, -4.77) * mm, "end": v(0.08, -4.7) * mm});
            skLineSegment(sketch, "E624", {"start": v(0.08, -4.7) * mm, "end": v(0.23, -4.63) * mm});
            skLineSegment(sketch, "E625", {"start": v(0.23, -4.63) * mm, "end": v(0.38, -4.54) * mm});
            skLineSegment(sketch, "E626", {"start": v(0.38, -4.54) * mm, "end": v(0.53, -4.45) * mm});
            skLineSegment(sketch, "E627", {"start": v(0.53, -4.45) * mm, "end": v(0.66, -4.37) * mm});
            skLineSegment(sketch, "E628", {"start": v(0.66, -4.37) * mm, "end": v(0.78, -4.3) * mm});
            skLineSegment(sketch, "E629", {"start": v(0.78, -4.3) * mm, "end": v(0.9, -4.2) * mm});
            skLineSegment(sketch, "E630", {"start": v(0.9, -4.2) * mm, "end": v(1.03, -4.1) * mm});
            skLineSegment(sketch, "E631", {"start": v(1.03, -4.1) * mm, "end": v(1.15, -4.01) * mm});
            skLineSegment(sketch, "E632", {"start": v(1.15, -4.01) * mm, "end": v(1.27, -3.9) * mm});
            skLineSegment(sketch, "E633", {"start": v(1.27, -3.9) * mm, "end": v(1.38, -3.8) * mm});
            skLineSegment(sketch, "E634", {"start": v(1.38, -3.8) * mm, "end": v(1.5, -3.7) * mm});
            skLineSegment(sketch, "E635", {"start": v(1.5, -3.7) * mm, "end": v(1.53, -3.72) * mm});
            skLineSegment(sketch, "E636", {"start": v(1.53, -3.72) * mm, "end": v(1.56, -3.75) * mm});
            skLineSegment(sketch, "E637", {"start": v(1.56, -3.75) * mm, "end": v(1.59, -3.79) * mm});
            skLineSegment(sketch, "E638", {"start": v(1.59, -3.79) * mm, "end": v(1.61, -3.82) * mm});
            skLineSegment(sketch, "E639", {"start": v(1.61, -3.82) * mm, "end": v(1.63, -3.86) * mm});
            skLineSegment(sketch, "E640", {"start": v(1.63, -3.86) * mm, "end": v(1.65, -3.9) * mm});
            skLineSegment(sketch, "E641", {"start": v(1.65, -3.9) * mm, "end": v(1.68, -3.99) * mm});
            skLineSegment(sketch, "E642", {"start": v(1.68, -3.99) * mm, "end": v(1.7, -4.06) * mm});
            skLineSegment(sketch, "E643", {"start": v(1.7, -4.06) * mm, "end": v(1.72, -4.15) * mm});
            skLineSegment(sketch, "E644", {"start": v(1.72, -4.15) * mm, "end": v(1.74, -4.25) * mm});
            skLineSegment(sketch, "E645", {"start": v(1.74, -4.25) * mm, "end": v(1.76, -4.36) * mm});
            skLineSegment(sketch, "E646", {"start": v(1.76, -4.36) * mm, "end": v(1.78, -4.47) * mm});
            skLineSegment(sketch, "E647", {"start": v(1.78, -4.47) * mm, "end": v(1.79, -4.6) * mm});
            skLineSegment(sketch, "E648", {"start": v(1.79, -4.6) * mm, "end": v(1.8, -4.73) * mm});
            skLineSegment(sketch, "E649", {"start": v(1.8, -4.73) * mm, "end": v(1.8, -4.86) * mm});
            skLineSegment(sketch, "E650", {"start": v(1.8, -4.86) * mm, "end": v(1.79, -5) * mm});
            skLineSegment(sketch, "E651", {"start": v(1.79, -5) * mm, "end": v(1.77, -5.16) * mm});
            skLineSegment(sketch, "E652", {"start": v(1.77, -5.16) * mm, "end": v(1.75, -5.3) * mm});
            skLineSegment(sketch, "E653", {"start": v(1.75, -5.3) * mm, "end": v(1.7, -5.46) * mm});
            skLineSegment(sketch, "E654", {"start": v(1.7, -5.46) * mm, "end": v(1.69, -5.54) * mm});
            skLineSegment(sketch, "E655", {"start": v(1.69, -5.54) * mm, "end": v(1.66, -5.62) * mm});
            skLineSegment(sketch, "E656", {"start": v(1.66, -5.62) * mm, "end": v(1.63, -5.7) * mm});
            skLineSegment(sketch, "E657", {"start": v(1.63, -5.7) * mm, "end": v(1.6, -5.79) * mm});
            skLineSegment(sketch, "E658", {"start": v(1.6, -5.79) * mm, "end": v(1.56, -5.87) * mm});
            skLineSegment(sketch, "E659", {"start": v(1.56, -5.87) * mm, "end": v(1.53, -5.95) * mm});
            skLineSegment(sketch, "E660", {"start": v(1.53, -5.95) * mm, "end": v(1.48, -6.03) * mm});
            skLineSegment(sketch, "E661", {"start": v(1.48, -6.03) * mm, "end": v(1.44, -6.12) * mm});
            skLineSegment(sketch, "E662", {"start": v(1.44, -6.12) * mm, "end": v(1.38, -6.22) * mm});
            skLineSegment(sketch, "E663", {"start": v(1.38, -6.22) * mm, "end": v(1.33, -6.32) * mm});
            skLineSegment(sketch, "E664", {"start": v(1.33, -6.32) * mm, "end": v(1.28, -6.43) * mm});
            skLineSegment(sketch, "E665", {"start": v(1.28, -6.43) * mm, "end": v(1.24, -6.53) * mm});
            skLineSegment(sketch, "E666", {"start": v(1.24, -6.53) * mm, "end": v(1.2, -6.64) * mm});
            skLineSegment(sketch, "E667", {"start": v(1.2, -6.64) * mm, "end": v(1.18, -6.75) * mm});
            skLineSegment(sketch, "E668", {"start": v(1.18, -6.75) * mm, "end": v(1.16, -6.85) * mm});
            skLineSegment(sketch, "E669", {"start": v(1.16, -6.85) * mm, "end": v(1.14, -6.96) * mm});
            skLineSegment(sketch, "E670", {"start": v(1.14, -6.96) * mm, "end": v(1.14, -7.06) * mm});
            skLineSegment(sketch, "E671", {"start": v(1.14, -7.06) * mm, "end": v(1.13, -7.17) * mm});
            skLineSegment(sketch, "E672", {"start": v(1.13, -7.17) * mm, "end": v(1.13, -7.27) * mm});
            skLineSegment(sketch, "E673", {"start": v(1.13, -7.27) * mm, "end": v(1.14, -7.37) * mm});
            skLineSegment(sketch, "E674", {"start": v(1.14, -7.37) * mm, "end": v(1.16, -7.48) * mm});
            skLineSegment(sketch, "E675", {"start": v(1.16, -7.48) * mm, "end": v(1.18, -7.58) * mm});
            skLineSegment(sketch, "E676", {"start": v(1.18, -7.58) * mm, "end": v(1.2, -7.68) * mm});
            skLineSegment(sketch, "E677", {"start": v(1.2, -7.68) * mm, "end": v(1.23, -7.78) * mm});
            skLineSegment(sketch, "E678", {"start": v(1.23, -7.78) * mm, "end": v(1.27, -7.88) * mm});
            skLineSegment(sketch, "E679", {"start": v(1.27, -7.88) * mm, "end": v(1.31, -7.97) * mm});
            skLineSegment(sketch, "E680", {"start": v(1.31, -7.97) * mm, "end": v(1.36, -8.07) * mm});
            skLineSegment(sketch, "E681", {"start": v(1.36, -8.07) * mm, "end": v(1.41, -8.16) * mm});
            skLineSegment(sketch, "E682", {"start": v(1.41, -8.16) * mm, "end": v(1.47, -8.25) * mm});
            skLineSegment(sketch, "E683", {"start": v(1.47, -8.25) * mm, "end": v(1.53, -8.34) * mm});
            skLineSegment(sketch, "E684", {"start": v(1.53, -8.34) * mm, "end": v(1.6, -8.43) * mm});
            skLineSegment(sketch, "E685", {"start": v(1.6, -8.43) * mm, "end": v(1.68, -8.51) * mm});
            skLineSegment(sketch, "E686", {"start": v(1.68, -8.51) * mm, "end": v(1.76, -8.6) * mm});
            skLineSegment(sketch, "E687", {"start": v(1.76, -8.6) * mm, "end": v(1.84, -8.67) * mm});
            skLineSegment(sketch, "E688", {"start": v(1.84, -8.67) * mm, "end": v(1.93, -8.75) * mm});
            skLineSegment(sketch, "E689", {"start": v(1.93, -8.75) * mm, "end": v(2.03, -8.82) * mm});
            skLineSegment(sketch, "E690", {"start": v(2.03, -8.82) * mm, "end": v(2.13, -8.9) * mm});
            skLineSegment(sketch, "E691", {"start": v(2.13, -8.9) * mm, "end": v(2.24, -8.96) * mm});
            skLineSegment(sketch, "E692", {"start": v(2.24, -8.96) * mm, "end": v(2.35, -9.02) * mm});
            skLineSegment(sketch, "E693", {"start": v(2.35, -9.02) * mm, "end": v(2.47, -9.09) * mm});
            skLineSegment(sketch, "E694", {"start": v(2.47, -9.09) * mm, "end": v(2.44, -9.1) * mm});
            skLineSegment(sketch, "E695", {"start": v(2.44, -9.1) * mm, "end": v(2.42, -9.1) * mm});
            skLineSegment(sketch, "E696", {"start": v(2.42, -9.1) * mm, "end": v(2.4, -9.12) * mm});
            skLineSegment(sketch, "E697", {"start": v(2.4, -9.12) * mm, "end": v(2.39, -9.13) * mm});
            skLineSegment(sketch, "E698", {"start": v(2.39, -9.13) * mm, "end": v(2.38, -9.15) * mm});
            skLineSegment(sketch, "E699", {"start": v(2.38, -9.15) * mm, "end": v(2.38, -9.18) * mm});
            skLineSegment(sketch, "E700", {"start": v(2.38, -9.18) * mm, "end": v(2.38, -9.21) * mm});
            skLineSegment(sketch, "E701", {"start": v(2.38, -9.21) * mm, "end": v(2.4, -9.25) * mm});
            skLineSegment(sketch, "E702", {"start": v(2.4, -9.25) * mm, "end": v(2.4, -9.27) * mm});
            skLineSegment(sketch, "E703", {"start": v(2.4, -9.27) * mm, "end": v(2.41, -9.29) * mm});
            skLineSegment(sketch, "E704", {"start": v(2.41, -9.29) * mm, "end": v(2.43, -9.3) * mm});
            skLineSegment(sketch, "E705", {"start": v(2.43, -9.3) * mm, "end": v(2.45, -9.33) * mm});
            skLineSegment(sketch, "E706", {"start": v(2.45, -9.33) * mm, "end": v(2.5, -9.37) * mm});
            skLineSegment(sketch, "E707", {"start": v(2.5, -9.37) * mm, "end": v(2.58, -9.41) * mm});
            skLineSegment(sketch, "E708", {"start": v(2.58, -9.41) * mm, "end": v(2.67, -9.46) * mm});
            skLineSegment(sketch, "E709", {"start": v(2.67, -9.46) * mm, "end": v(2.77, -9.5) * mm});
            skLineSegment(sketch, "E710", {"start": v(2.77, -9.5) * mm, "end": v(2.9, -9.53) * mm});
            skLineSegment(sketch, "E711", {"start": v(2.9, -9.53) * mm, "end": v(3.03, -9.56) * mm});
            skLineSegment(sketch, "E712", {"start": v(3.03, -9.56) * mm, "end": v(3.18, -9.59) * mm});
            skLineSegment(sketch, "E713", {"start": v(3.18, -9.59) * mm, "end": v(3.34, -9.6) * mm});
            skLineSegment(sketch, "E714", {"start": v(3.34, -9.6) * mm, "end": v(3.43, -9.6) * mm});
            skLineSegment(sketch, "E715", {"start": v(3.43, -9.6) * mm, "end": v(3.52, -9.6) * mm});
            skLineSegment(sketch, "E716", {"start": v(3.52, -9.6) * mm, "end": v(3.6, -9.6) * mm});
            skLineSegment(sketch, "E717", {"start": v(3.6, -9.6) * mm, "end": v(3.7, -9.6) * mm});
            skLineSegment(sketch, "E718", {"start": v(3.7, -9.6) * mm, "end": v(3.8, -9.6) * mm});
            skLineSegment(sketch, "E719", {"start": v(3.8, -9.6) * mm, "end": v(3.9, -9.58) * mm});
            skLineSegment(sketch, "E720", {"start": v(3.9, -9.58) * mm, "end": v(4, -9.57) * mm});
            skLineSegment(sketch, "E721", {"start": v(4, -9.57) * mm, "end": v(4.12, -9.55) * mm});
            skLineSegment(sketch, "E722", {"start": v(4.12, -9.55) * mm, "end": v(4.23, -9.53) * mm});
            skLineSegment(sketch, "E723", {"start": v(4.23, -9.53) * mm, "end": v(4.34, -9.5) * mm});
            skLineSegment(sketch, "E724", {"start": v(4.34, -9.5) * mm, "end": v(4.45, -9.48) * mm});
            skLineSegment(sketch, "E725", {"start": v(4.45, -9.48) * mm, "end": v(4.57, -9.44) * mm});
            skLineSegment(sketch, "E726", {"start": v(4.57, -9.44) * mm, "end": v(4.38, -9.44) * mm});
            skLineSegment(sketch, "E727", {"start": v(4.38, -9.44) * mm, "end": v(4.21, -9.42) * mm});
            skLineSegment(sketch, "E728", {"start": v(4.21, -9.42) * mm, "end": v(4.05, -9.4) * mm});
            skLineSegment(sketch, "E729", {"start": v(4.05, -9.4) * mm, "end": v(3.9, -9.38) * mm});
            skLineSegment(sketch, "E730", {"start": v(3.9, -9.38) * mm, "end": v(3.77, -9.36) * mm});
            skLineSegment(sketch, "E731", {"start": v(3.77, -9.36) * mm, "end": v(3.65, -9.33) * mm});
            skLineSegment(sketch, "E732", {"start": v(3.65, -9.33) * mm, "end": v(3.54, -9.3) * mm});
            skLineSegment(sketch, "E733", {"start": v(3.54, -9.3) * mm, "end": v(3.45, -9.26) * mm});
            skLineSegment(sketch, "E734", {"start": v(3.45, -9.26) * mm, "end": v(3.36, -9.22) * mm});
            skLineSegment(sketch, "E735", {"start": v(3.36, -9.22) * mm, "end": v(3.28, -9.18) * mm});
            skLineSegment(sketch, "E736", {"start": v(3.28, -9.18) * mm, "end": v(3.22, -9.13) * mm});
            skLineSegment(sketch, "E737", {"start": v(3.22, -9.13) * mm, "end": v(3.16, -9.09) * mm});
            skLineSegment(sketch, "E738", {"start": v(3.16, -9.09) * mm, "end": v(3.12, -9.04) * mm});
            skLineSegment(sketch, "E739", {"start": v(3.12, -9.04) * mm, "end": v(3.08, -9) * mm});
            skLineSegment(sketch, "E740", {"start": v(3.08, -9) * mm, "end": v(3.05, -8.95) * mm});
            skLineSegment(sketch, "E741", {"start": v(3.05, -8.95) * mm, "end": v(3.03, -8.9) * mm});
            skLineSegment(sketch, "E742", {"start": v(3.03, -8.9) * mm, "end": v(3.02, -8.87) * mm});
            skLineSegment(sketch, "E743", {"start": v(3.02, -8.87) * mm, "end": v(3, -8.85) * mm});
            skLineSegment(sketch, "E744", {"start": v(3, -8.85) * mm, "end": v(2.99, -8.82) * mm});
            skLineSegment(sketch, "E745", {"start": v(2.99, -8.82) * mm, "end": v(2.97, -8.8) * mm});
            skLineSegment(sketch, "E746", {"start": v(2.97, -8.8) * mm, "end": v(2.95, -8.79) * mm});
            skLineSegment(sketch, "E747", {"start": v(2.95, -8.79) * mm, "end": v(2.93, -8.77) * mm});
            skLineSegment(sketch, "E748", {"start": v(2.93, -8.77) * mm, "end": v(2.9, -8.76) * mm});
            skLineSegment(sketch, "E749", {"start": v(2.9, -8.76) * mm, "end": v(2.88, -8.75) * mm});
            skLineSegment(sketch, "E750", {"start": v(2.88, -8.75) * mm, "end": v(2.82, -8.74) * mm});
            skLineSegment(sketch, "E751", {"start": v(2.82, -8.74) * mm, "end": v(2.77, -8.73) * mm});
            skLineSegment(sketch, "E752", {"start": v(2.77, -8.73) * mm, "end": v(2.7, -8.74) * mm});
            skLineSegment(sketch, "E753", {"start": v(2.7, -8.74) * mm, "end": v(2.65, -8.75) * mm});
            skLineSegment(sketch, "E754", {"start": v(2.65, -8.75) * mm, "end": v(2.62, -8.76) * mm});
            skLineSegment(sketch, "E755", {"start": v(2.62, -8.76) * mm, "end": v(2.6, -8.77) * mm});
            skLineSegment(sketch, "E756", {"start": v(2.6, -8.77) * mm, "end": v(2.59, -8.78) * mm});
            skLineSegment(sketch, "E757", {"start": v(2.59, -8.78) * mm, "end": v(2.57, -8.8) * mm});
            skLineSegment(sketch, "E758", {"start": v(2.57, -8.8) * mm, "end": v(2.56, -8.81) * mm});
            skLineSegment(sketch, "E759", {"start": v(2.56, -8.81) * mm, "end": v(2.55, -8.83) * mm});
            skLineSegment(sketch, "E760", {"start": v(2.55, -8.83) * mm, "end": v(2.55, -8.85) * mm});
            skLineSegment(sketch, "E761", {"start": v(2.55, -8.85) * mm, "end": v(2.55, -8.87) * mm});
            skLineSegment(sketch, "E762", {"start": v(2.55, -8.87) * mm, "end": v(2.45, -8.8) * mm});
            skLineSegment(sketch, "E763", {"start": v(2.45, -8.8) * mm, "end": v(2.35, -8.71) * mm});
            skLineSegment(sketch, "E764", {"start": v(2.35, -8.71) * mm, "end": v(2.27, -8.63) * mm});
            skLineSegment(sketch, "E765", {"start": v(2.27, -8.63) * mm, "end": v(2.2, -8.55) * mm});
            skLineSegment(sketch, "E766", {"start": v(2.2, -8.55) * mm, "end": v(2.12, -8.47) * mm});
            skLineSegment(sketch, "E767", {"start": v(2.12, -8.47) * mm, "end": v(2.05, -8.4) * mm});
            skLineSegment(sketch, "E768", {"start": v(2.05, -8.4) * mm, "end": v(2, -8.31) * mm});
            skLineSegment(sketch, "E769", {"start": v(2, -8.31) * mm, "end": v(1.94, -8.24) * mm});
            skLineSegment(sketch, "E770", {"start": v(1.94, -8.24) * mm, "end": v(1.9, -8.16) * mm});
            skLineSegment(sketch, "E771", {"start": v(1.9, -8.16) * mm, "end": v(1.86, -8.08) * mm});
            skLineSegment(sketch, "E772", {"start": v(1.86, -8.08) * mm, "end": v(1.82, -8) * mm});
            skLineSegment(sketch, "E773", {"start": v(1.82, -8) * mm, "end": v(1.8, -7.92) * mm});
            skLineSegment(sketch, "E774", {"start": v(1.8, -7.92) * mm, "end": v(1.77, -7.84) * mm});
            skLineSegment(sketch, "E775", {"start": v(1.77, -7.84) * mm, "end": v(1.76, -7.77) * mm});
            skLineSegment(sketch, "E776", {"start": v(1.76, -7.77) * mm, "end": v(1.74, -7.69) * mm});
            skLineSegment(sketch, "E777", {"start": v(1.74, -7.69) * mm, "end": v(1.74, -7.6) * mm});
            skLineSegment(sketch, "E778", {"start": v(1.74, -7.6) * mm, "end": v(1.73, -7.53) * mm});
            skLineSegment(sketch, "E779", {"start": v(1.73, -7.53) * mm, "end": v(1.73, -7.45) * mm});
            skLineSegment(sketch, "E780", {"start": v(1.73, -7.45) * mm, "end": v(1.74, -7.37) * mm});
            skLineSegment(sketch, "E781", {"start": v(1.74, -7.37) * mm, "end": v(1.75, -7.28) * mm});
            skLineSegment(sketch, "E782", {"start": v(1.75, -7.28) * mm, "end": v(1.77, -7.2) * mm});
            skLineSegment(sketch, "E783", {"start": v(1.77, -7.2) * mm, "end": v(1.79, -7.12) * mm});
            skLineSegment(sketch, "E784", {"start": v(1.79, -7.12) * mm, "end": v(1.8, -7.03) * mm});
            skLineSegment(sketch, "E785", {"start": v(1.8, -7.03) * mm, "end": v(1.84, -6.95) * mm});
            skLineSegment(sketch, "E786", {"start": v(1.84, -6.95) * mm, "end": v(1.87, -6.86) * mm});
            skLineSegment(sketch, "E787", {"start": v(1.87, -6.86) * mm, "end": v(1.9, -6.77) * mm});
            skLineSegment(sketch, "E788", {"start": v(1.9, -6.77) * mm, "end": v(1.97, -6.6) * mm});
            skLineSegment(sketch, "E789", {"start": v(1.97, -6.6) * mm, "end": v(2.06, -6.41) * mm});
            skLineSegment(sketch, "E790", {"start": v(2.06, -6.41) * mm, "end": v(2.16, -6.22) * mm});
            skLineSegment(sketch, "E791", {"start": v(2.16, -6.22) * mm, "end": v(2.26, -6.02) * mm});
            skLineSegment(sketch, "E792", {"start": v(2.26, -6.02) * mm, "end": v(2.35, -5.82) * mm});
            skLineSegment(sketch, "E793", {"start": v(2.35, -5.82) * mm, "end": v(2.42, -5.63) * mm});
            skLineSegment(sketch, "E794", {"start": v(2.42, -5.63) * mm, "end": v(2.49, -5.43) * mm});
            skLineSegment(sketch, "E795", {"start": v(2.49, -5.43) * mm, "end": v(2.54, -5.24) * mm});
            skLineSegment(sketch, "E796", {"start": v(2.54, -5.24) * mm, "end": v(2.56, -5.15) * mm});
            skLineSegment(sketch, "E797", {"start": v(2.56, -5.15) * mm, "end": v(2.58, -5.05) * mm});
            skLineSegment(sketch, "E798", {"start": v(2.58, -5.05) * mm, "end": v(2.6, -4.96) * mm});
            skLineSegment(sketch, "E799", {"start": v(2.6, -4.96) * mm, "end": v(2.61, -4.87) * mm});
            skLineSegment(sketch, "E800", {"start": v(2.61, -4.87) * mm, "end": v(2.62, -4.77) * mm});
            skLineSegment(sketch, "E801", {"start": v(2.62, -4.77) * mm, "end": v(2.63, -4.68) * mm});
            skLineSegment(sketch, "E802", {"start": v(2.63, -4.68) * mm, "end": v(2.64, -4.6) * mm});
            skLineSegment(sketch, "E803", {"start": v(2.64, -4.6) * mm, "end": v(2.64, -4.5) * mm});
            skLineSegment(sketch, "E804", {"start": v(2.64, -4.5) * mm, "end": v(2.64, -4.41) * mm});
            skLineSegment(sketch, "E805", {"start": v(2.64, -4.41) * mm, "end": v(2.64, -4.32) * mm});
            skLineSegment(sketch, "E806", {"start": v(2.64, -4.32) * mm, "end": v(2.63, -4.23) * mm});
            skLineSegment(sketch, "E807", {"start": v(2.63, -4.23) * mm, "end": v(2.63, -4.15) * mm});
            skLineSegment(sketch, "E808", {"start": v(2.63, -4.15) * mm, "end": v(2.62, -4.06) * mm});
            skLineSegment(sketch, "E809", {"start": v(2.62, -4.06) * mm, "end": v(2.6, -3.97) * mm});
            skLineSegment(sketch, "E810", {"start": v(2.6, -3.97) * mm, "end": v(2.59, -3.89) * mm});
            skLineSegment(sketch, "E811", {"start": v(2.59, -3.89) * mm, "end": v(2.57, -3.8) * mm});
            skLineSegment(sketch, "E812", {"start": v(2.57, -3.8) * mm, "end": v(2.55, -3.72) * mm});
            skLineSegment(sketch, "E813", {"start": v(2.55, -3.72) * mm, "end": v(2.52, -3.64) * mm});
            skLineSegment(sketch, "E814", {"start": v(2.52, -3.64) * mm, "end": v(2.5, -3.56) * mm});
            skLineSegment(sketch, "E815", {"start": v(2.5, -3.56) * mm, "end": v(2.47, -3.48) * mm});
            skLineSegment(sketch, "E816", {"start": v(2.47, -3.48) * mm, "end": v(2.44, -3.4) * mm});
            skLineSegment(sketch, "E817", {"start": v(2.44, -3.4) * mm, "end": v(2.4, -3.32) * mm});
            skLineSegment(sketch, "E818", {"start": v(2.4, -3.32) * mm, "end": v(2.38, -3.26) * mm});
            skLineSegment(sketch, "E819", {"start": v(2.38, -3.26) * mm, "end": v(2.35, -3.21) * mm});
            skLineSegment(sketch, "E820", {"start": v(2.35, -3.21) * mm, "end": v(2.32, -3.16) * mm});
            skLineSegment(sketch, "E821", {"start": v(2.32, -3.16) * mm, "end": v(2.29, -3.1) * mm});
            skLineSegment(sketch, "E822", {"start": v(2.29, -3.1) * mm, "end": v(2.21, -3.01) * mm});
            skLineSegment(sketch, "E823", {"start": v(2.21, -3.01) * mm, "end": v(2.14, -2.92) * mm});
            skLineSegment(sketch, "E824", {"start": v(2.14, -2.92) * mm, "end": v(2.25, -2.74) * mm});
            skLineSegment(sketch, "E825", {"start": v(2.25, -2.74) * mm, "end": v(2.36, -2.56) * mm});
            skLineSegment(sketch, "E826", {"start": v(2.36, -2.56) * mm, "end": v(2.46, -2.37) * mm});
            skLineSegment(sketch, "E827", {"start": v(2.46, -2.37) * mm, "end": v(2.56, -2.18) * mm});
            skLineSegment(sketch, "E828", {"start": v(2.56, -2.18) * mm, "end": v(2.64, -1.99) * mm});
            skLineSegment(sketch, "E829", {"start": v(2.64, -1.99) * mm, "end": v(2.72, -1.79) * mm});
            skLineSegment(sketch, "E830", {"start": v(2.72, -1.79) * mm, "end": v(2.8, -1.58) * mm});
            skLineSegment(sketch, "E831", {"start": v(2.8, -1.58) * mm, "end": v(2.85, -1.37) * mm});
            skLineSegment(sketch, "E832", {"start": v(2.85, -1.37) * mm, "end": v(2.92, -1.4) * mm});
            skLineSegment(sketch, "E833", {"start": v(2.92, -1.4) * mm, "end": v(2.99, -1.43) * mm});
            skLineSegment(sketch, "E834", {"start": v(2.99, -1.43) * mm, "end": v(3.03, -1.44) * mm});
            skLineSegment(sketch, "E835", {"start": v(3.03, -1.44) * mm, "end": v(3.07, -1.45) * mm});
            skLineSegment(sketch, "E836", {"start": v(3.07, -1.45) * mm, "end": v(3.12, -1.46) * mm});
            skLineSegment(sketch, "E837", {"start": v(3.12, -1.46) * mm, "end": v(3.16, -1.46) * mm});
            skLineSegment(sketch, "E838", {"start": v(3.16, -1.46) * mm, "end": v(3.22, -1.47) * mm});
            skLineSegment(sketch, "E839", {"start": v(3.22, -1.47) * mm, "end": v(3.27, -1.47) * mm});
            skLineSegment(sketch, "E840", {"start": v(3.27, -1.47) * mm, "end": v(3.33, -1.46) * mm});
            skLineSegment(sketch, "E841", {"start": v(3.33, -1.46) * mm, "end": v(3.39, -1.46) * mm});
            skLineSegment(sketch, "E842", {"start": v(3.39, -1.46) * mm, "end": v(3.45, -1.45) * mm});
            skLineSegment(sketch, "E843", {"start": v(3.45, -1.45) * mm, "end": v(3.52, -1.43) * mm});
            skLineSegment(sketch, "E844", {"start": v(3.52, -1.43) * mm, "end": v(3.6, -1.41) * mm});
            skLineSegment(sketch, "E845", {"start": v(3.6, -1.41) * mm, "end": v(3.68, -1.39) * mm});
            skLineSegment(sketch, "E846", {"start": v(3.68, -1.39) * mm, "end": v(3.53, -1.34) * mm});
            skLineSegment(sketch, "E847", {"start": v(3.53, -1.34) * mm, "end": v(3.41, -1.3) * mm});
            skLineSegment(sketch, "E848", {"start": v(3.41, -1.3) * mm, "end": v(3.3, -1.24) * mm});
            skLineSegment(sketch, "E849", {"start": v(3.3, -1.24) * mm, "end": v(3.21, -1.2) * mm});
            skLineSegment(sketch, "E850", {"start": v(3.21, -1.2) * mm, "end": v(3.13, -1.14) * mm});
            skLineSegment(sketch, "E851", {"start": v(3.13, -1.14) * mm, "end": v(3.07, -1.09) * mm});
            skLineSegment(sketch, "E852", {"start": v(3.07, -1.09) * mm, "end": v(3, -1.02) * mm});
            skLineSegment(sketch, "E853", {"start": v(3, -1.02) * mm, "end": v(2.95, -0.95) * mm});
            skLineSegment(sketch, "E854", {"start": v(2.95, -0.95) * mm, "end": v(2.98, -0.77) * mm});
            skLineSegment(sketch, "E855", {"start": v(2.98, -0.77) * mm, "end": v(3, -0.6) * mm});
            skLineSegment(sketch, "E856", {"start": v(3, -0.6) * mm, "end": v(3.01, -0.42) * mm});
            skLineSegment(sketch, "E857", {"start": v(3.01, -0.42) * mm, "end": v(3.02, -0.25) * mm});
            skLineSegment(sketch, "E858", {"start": v(3.02, -0.25) * mm, "end": v(3.08, -0.26) * mm});
            skLineSegment(sketch, "E859", {"start": v(3.08, -0.26) * mm, "end": v(3.16, -0.26) * mm});
            skLineSegment(sketch, "E860", {"start": v(3.16, -0.26) * mm, "end": v(3.24, -0.26) * mm});
            skLineSegment(sketch, "E861", {"start": v(3.24, -0.26) * mm, "end": v(3.33, -0.24) * mm});
            skLineSegment(sketch, "E862", {"start": v(3.33, -0.24) * mm, "end": v(3.37, -0.23) * mm});
            skLineSegment(sketch, "E863", {"start": v(3.37, -0.23) * mm, "end": v(3.42, -0.21) * mm});
            skLineSegment(sketch, "E864", {"start": v(3.42, -0.21) * mm, "end": v(3.48, -0.2) * mm});
            skLineSegment(sketch, "E865", {"start": v(3.48, -0.2) * mm, "end": v(3.53, -0.17) * mm});
            skLineSegment(sketch, "E866", {"start": v(3.53, -0.17) * mm, "end": v(3.59, -0.14) * mm});
            skLineSegment(sketch, "E867", {"start": v(3.59, -0.14) * mm, "end": v(3.64, -0.11) * mm});
            skLineSegment(sketch, "E868", {"start": v(3.64, -0.11) * mm, "end": v(3.7, -0.07) * mm});
            skLineSegment(sketch, "E869", {"start": v(3.7, -0.07) * mm, "end": v(3.77, -0.03) * mm});
            skLineSegment(sketch, "E870", {"start": v(3.77, -0.03) * mm, "end": v(3.63, -0.03) * mm});
            skLineSegment(sketch, "E871", {"start": v(3.63, -0.03) * mm, "end": v(3.5, -0.01) * mm});
            skLineSegment(sketch, "E872", {"start": v(3.5, -0.01) * mm, "end": v(3.4, 0) * mm});
            skLineSegment(sketch, "E873", {"start": v(3.4, 0) * mm, "end": v(3.3, 0.02) * mm});
            skLineSegment(sketch, "E874", {"start": v(3.3, 0.02) * mm, "end": v(3.21, 0.04) * mm});
            skLineSegment(sketch, "E875", {"start": v(3.21, 0.04) * mm, "end": v(3.14, 0.07) * mm});
            skLineSegment(sketch, "E876", {"start": v(3.14, 0.07) * mm, "end": v(3.06, 0.1) * mm});
            skLineSegment(sketch, "E877", {"start": v(3.06, 0.1) * mm, "end": v(3, 0.15) * mm});
            skLineSegment(sketch, "E878", {"start": v(3, 0.15) * mm, "end": v(2.98, 0.25) * mm});
            skLineSegment(sketch, "E879", {"start": v(2.98, 0.25) * mm, "end": v(2.97, 0.35) * mm});
            skLineSegment(sketch, "E880", {"start": v(2.97, 0.35) * mm, "end": v(2.93, 0.53) * mm});
            skLineSegment(sketch, "E881", {"start": v(2.93, 0.53) * mm, "end": v(2.89, 0.71) * mm});
            skLineSegment(sketch, "E882", {"start": v(2.89, 0.71) * mm, "end": v(2.84, 0.88) * mm});
            skLineSegment(sketch, "E883", {"start": v(2.84, 0.88) * mm, "end": v(2.9, 0.9) * mm});
            skLineSegment(sketch, "E884", {"start": v(2.9, 0.9) * mm, "end": v(2.98, 0.91) * mm});
            skLineSegment(sketch, "E885", {"start": v(2.98, 0.91) * mm, "end": v(3.06, 0.94) * mm});
            skLineSegment(sketch, "E886", {"start": v(3.06, 0.94) * mm, "end": v(3.1, 0.96) * mm});
            skLineSegment(sketch, "E887", {"start": v(3.1, 0.96) * mm, "end": v(3.14, 0.99) * mm});
            skLineSegment(sketch, "E888", {"start": v(3.14, 0.99) * mm, "end": v(3.18, 1.01) * mm});
            skLineSegment(sketch, "E889", {"start": v(3.18, 1.01) * mm, "end": v(3.22, 1.05) * mm});
            skLineSegment(sketch, "E890", {"start": v(3.22, 1.05) * mm, "end": v(3.27, 1.08) * mm});
            skLineSegment(sketch, "E891", {"start": v(3.27, 1.08) * mm, "end": v(3.31, 1.12) * mm});
            skLineSegment(sketch, "E892", {"start": v(3.31, 1.12) * mm, "end": v(3.36, 1.17) * mm});
            skLineSegment(sketch, "E893", {"start": v(3.36, 1.17) * mm, "end": v(3.4, 1.22) * mm});
            skLineSegment(sketch, "E894", {"start": v(3.4, 1.22) * mm, "end": v(3.46, 1.28) * mm});
            skLineSegment(sketch, "E895", {"start": v(3.46, 1.28) * mm, "end": v(3.5, 1.34) * mm});
            skLineSegment(sketch, "E896", {"start": v(3.5, 1.34) * mm, "end": v(3.37, 1.3) * mm});
            skLineSegment(sketch, "E897", {"start": v(3.37, 1.3) * mm, "end": v(3.24, 1.27) * mm});
            skLineSegment(sketch, "E898", {"start": v(3.24, 1.27) * mm, "end": v(3.13, 1.25) * mm});
            skLineSegment(sketch, "E899", {"start": v(3.13, 1.25) * mm, "end": v(3.03, 1.23) * mm});
            skLineSegment(sketch, "E900", {"start": v(3.03, 1.23) * mm, "end": v(2.94, 1.23) * mm});
            skLineSegment(sketch, "E901", {"start": v(2.94, 1.23) * mm, "end": v(2.85, 1.23) * mm});
            skLineSegment(sketch, "E902", {"start": v(2.85, 1.23) * mm, "end": v(2.77, 1.25) * mm});
            skLineSegment(sketch, "E903", {"start": v(2.77, 1.25) * mm, "end": v(2.68, 1.27) * mm});
            skLineSegment(sketch, "E904", {"start": v(2.68, 1.27) * mm, "end": v(2.64, 1.35) * mm});
            skLineSegment(sketch, "E905", {"start": v(2.64, 1.35) * mm, "end": v(2.6, 1.42) * mm});
            skLineSegment(sketch, "E906", {"start": v(2.6, 1.42) * mm, "end": v(2.56, 1.5) * mm});
            skLineSegment(sketch, "E907", {"start": v(2.56, 1.5) * mm, "end": v(2.52, 1.57) * mm});
            skLineSegment(sketch, "E908", {"start": v(2.52, 1.57) * mm, "end": v(2.47, 1.63) * mm});
            skLineSegment(sketch, "E909", {"start": v(2.47, 1.63) * mm, "end": v(2.42, 1.7) * mm});
            skLineSegment(sketch, "E910", {"start": v(2.42, 1.7) * mm, "end": v(2.37, 1.77) * mm});
            skLineSegment(sketch, "E911", {"start": v(2.37, 1.77) * mm, "end": v(2.32, 1.83) * mm});
            skLineSegment(sketch, "E912", {"start": v(2.32, 1.83) * mm, "end": v(2.38, 1.88) * mm});
            skLineSegment(sketch, "E913", {"start": v(2.38, 1.88) * mm, "end": v(2.43, 1.93) * mm});
            skLineSegment(sketch, "E914", {"start": v(2.43, 1.93) * mm, "end": v(2.46, 1.96) * mm});
            skLineSegment(sketch, "E915", {"start": v(2.46, 1.96) * mm, "end": v(2.48, 2) * mm});
            skLineSegment(sketch, "E916", {"start": v(2.48, 2) * mm, "end": v(2.5, 2.04) * mm});
            skLineSegment(sketch, "E917", {"start": v(2.5, 2.04) * mm, "end": v(2.53, 2.08) * mm});
            skLineSegment(sketch, "E918", {"start": v(2.53, 2.08) * mm, "end": v(2.56, 2.13) * mm});
            skLineSegment(sketch, "E919", {"start": v(2.56, 2.13) * mm, "end": v(2.58, 2.18) * mm});
            skLineSegment(sketch, "E920", {"start": v(2.58, 2.18) * mm, "end": v(2.6, 2.24) * mm});
            skLineSegment(sketch, "E921", {"start": v(2.6, 2.24) * mm, "end": v(2.61, 2.3) * mm});
            skLineSegment(sketch, "E922", {"start": v(2.61, 2.3) * mm, "end": v(2.63, 2.36) * mm});
            skLineSegment(sketch, "E923", {"start": v(2.63, 2.36) * mm, "end": v(2.64, 2.44) * mm});
            skLineSegment(sketch, "E924", {"start": v(2.64, 2.44) * mm, "end": v(2.65, 2.51) * mm});
            skLineSegment(sketch, "E925", {"start": v(2.65, 2.51) * mm, "end": v(2.66, 2.6) * mm});
            skLineSegment(sketch, "E926", {"start": v(2.66, 2.6) * mm, "end": v(2.57, 2.5) * mm});
            skLineSegment(sketch, "E927", {"start": v(2.57, 2.5) * mm, "end": v(2.48, 2.4) * mm});
            skLineSegment(sketch, "E928", {"start": v(2.48, 2.4) * mm, "end": v(2.4, 2.32) * mm});
            skLineSegment(sketch, "E929", {"start": v(2.4, 2.32) * mm, "end": v(2.33, 2.26) * mm});
            skLineSegment(sketch, "E930", {"start": v(2.33, 2.26) * mm, "end": v(2.25, 2.2) * mm});
            skLineSegment(sketch, "E931", {"start": v(2.25, 2.2) * mm, "end": v(2.18, 2.16) * mm});
            skLineSegment(sketch, "E932", {"start": v(2.18, 2.16) * mm, "end": v(2.1, 2.12) * mm});
            skLineSegment(sketch, "E933", {"start": v(2.1, 2.12) * mm, "end": v(2.03, 2.1) * mm});
            skLineSegment(sketch, "E934", {"start": v(2.03, 2.1) * mm, "end": v(1.95, 2.15) * mm});
            skLineSegment(sketch, "E935", {"start": v(1.95, 2.15) * mm, "end": v(1.88, 2.2) * mm});
            skLineSegment(sketch, "E936", {"start": v(1.88, 2.2) * mm, "end": v(1.8, 2.25) * mm});
            skLineSegment(sketch, "E937", {"start": v(1.8, 2.25) * mm, "end": v(1.71, 2.3) * mm});
            skLineSegment(sketch, "E938", {"start": v(1.71, 2.3) * mm, "end": v(1.63, 2.34) * mm});
            skLineSegment(sketch, "E939", {"start": v(1.63, 2.34) * mm, "end": v(1.54, 2.38) * mm});
            skLineSegment(sketch, "E940", {"start": v(1.54, 2.38) * mm, "end": v(1.45, 2.41) * mm});
            skLineSegment(sketch, "E941", {"start": v(1.45, 2.41) * mm, "end": v(1.35, 2.45) * mm});
            skLineSegment(sketch, "E942", {"start": v(1.35, 2.45) * mm, "end": v(1.38, 2.5) * mm});
            skLineSegment(sketch, "E943", {"start": v(1.38, 2.5) * mm, "end": v(1.4, 2.58) * mm});
            skLineSegment(sketch, "E944", {"start": v(1.4, 2.58) * mm, "end": v(1.4, 2.66) * mm});
            skLineSegment(sketch, "E945", {"start": v(1.4, 2.66) * mm, "end": v(1.41, 2.75) * mm});
            skLineSegment(sketch, "E946", {"start": v(1.41, 2.75) * mm, "end": v(1.4, 2.84) * mm});
            skLineSegment(sketch, "E947", {"start": v(1.4, 2.84) * mm, "end": v(1.39, 2.95) * mm});
            skLineSegment(sketch, "E948", {"start": v(1.39, 2.95) * mm, "end": v(1.36, 3.07) * mm});
            skLineSegment(sketch, "E949", {"start": v(1.36, 3.07) * mm, "end": v(1.32, 3.2) * mm});
            skLineSegment(sketch, "E950", {"start": v(1.32, 3.2) * mm, "end": v(1.28, 3.09) * mm});
            skLineSegment(sketch, "E951", {"start": v(1.28, 3.09) * mm, "end": v(1.24, 2.98) * mm});
            skLineSegment(sketch, "E952", {"start": v(1.24, 2.98) * mm, "end": v(1.2, 2.88) * mm});
            skLineSegment(sketch, "E953", {"start": v(1.2, 2.88) * mm, "end": v(1.17, 2.8) * mm});
            skLineSegment(sketch, "E954", {"start": v(1.17, 2.8) * mm, "end": v(1.13, 2.72) * mm});
            skLineSegment(sketch, "E955", {"start": v(1.13, 2.72) * mm, "end": v(1.09, 2.66) * mm});
            skLineSegment(sketch, "E956", {"start": v(1.09, 2.66) * mm, "end": v(1.04, 2.6) * mm});
            skLineSegment(sketch, "E957", {"start": v(1.04, 2.6) * mm, "end": v(0.99, 2.54) * mm});
            skLineSegment(sketch, "E958", {"start": v(0.99, 2.54) * mm, "end": v(0.8, 2.57) * mm});
            skLineSegment(sketch, "E959", {"start": v(0.8, 2.57) * mm, "end": v(0.62, 2.6) * mm});
            skLineSegment(sketch, "E960", {"start": v(0.62, 2.6) * mm, "end": v(0.42, 2.6) * mm});
            skLineSegment(sketch, "E961", {"start": v(0.42, 2.6) * mm, "end": v(0.2, 2.6) * mm});
            skLineSegment(sketch, "E962", {"start": v(0.2, 2.6) * mm, "end": v(0.2, 2.67) * mm});
            skLineSegment(sketch, "E963", {"start": v(0.2, 2.67) * mm, "end": v(0.2, 2.73) * mm});
            skLineSegment(sketch, "E964", {"start": v(0.2, 2.73) * mm, "end": v(0.2, 2.8) * mm});
            skLineSegment(sketch, "E965", {"start": v(0.2, 2.8) * mm, "end": v(0.19, 2.88) * mm});
            skLineSegment(sketch, "E966", {"start": v(0.19, 2.88) * mm, "end": v(0.16, 2.96) * mm});
            skLineSegment(sketch, "E967", {"start": v(0.16, 2.96) * mm, "end": v(0.14, 3.04) * mm});
            skLineSegment(sketch, "E968", {"start": v(0.14, 3.04) * mm, "end": v(0.1, 3.14) * mm});
            skLineSegment(sketch, "E969", {"start": v(0.1, 3.14) * mm, "end": v(0.05, 3.24) * mm});
            skLineSegment(sketch, "E970", {"start": v(0.05, 3.24) * mm, "end": v(0.01, 3.03) * mm});
            skLineSegment(sketch, "E971", {"start": v(0.01, 3.03) * mm, "end": v(0, 2.94) * mm});
            skLineSegment(sketch, "E972", {"start": v(0, 2.94) * mm, "end": v(-0.03, 2.86) * mm});
            skLineSegment(sketch, "E973", {"start": v(-0.03, 2.86) * mm, "end": v(-0.06, 2.79) * mm});
            skLineSegment(sketch, "E974", {"start": v(-0.06, 2.79) * mm, "end": v(-0.08, 2.72) * mm});
            skLineSegment(sketch, "E975", {"start": v(-0.08, 2.72) * mm, "end": v(-0.11, 2.66) * mm});
            skLineSegment(sketch, "E976", {"start": v(-0.11, 2.66) * mm, "end": v(-0.14, 2.6) * mm});
            skLineSegment(sketch, "E977", {"start": v(-0.14, 2.6) * mm, "end": v(-0.34, 2.6) * mm});
            skLineSegment(sketch, "E978", {"start": v(-0.34, 2.6) * mm, "end": v(-0.52, 2.6) * mm});
            skLineSegment(sketch, "E979", {"start": v(-0.52, 2.6) * mm, "end": v(-0.7, 2.61) * mm});
            skLineSegment(sketch, "E980", {"start": v(-0.7, 2.61) * mm, "end": v(-0.86, 2.62) * mm});
            skLineSegment(sketch, "E981", {"start": v(-0.86, 2.62) * mm, "end": v(-0.84, 2.68) * mm});
            skLineSegment(sketch, "E982", {"start": v(-0.84, 2.68) * mm, "end": v(-0.82, 2.75) * mm});
            skLineSegment(sketch, "E983", {"start": v(-0.82, 2.75) * mm, "end": v(-0.8, 2.83) * mm});
            skLineSegment(sketch, "E984", {"start": v(-0.8, 2.83) * mm, "end": v(-0.8, 2.9) * mm});
            skLineSegment(sketch, "E985", {"start": v(-0.8, 2.9) * mm, "end": v(-0.8, 3) * mm});
            skLineSegment(sketch, "E986", {"start": v(-0.8, 3) * mm, "end": v(-0.82, 3.1) * mm});
            skLineSegment(sketch, "E987", {"start": v(-0.82, 3.1) * mm, "end": v(-0.84, 3.22) * mm});
            skLineSegment(sketch, "E988", {"start": v(-0.84, 3.22) * mm, "end": v(-0.87, 3.34) * mm});
            skLineSegment(sketch, "E989", {"start": v(-0.87, 3.34) * mm, "end": v(-0.92, 3.22) * mm});
            skLineSegment(sketch, "E990", {"start": v(-0.92, 3.22) * mm, "end": v(-0.96, 3.1) * mm});
            skLineSegment(sketch, "E991", {"start": v(-0.96, 3.1) * mm, "end": v(-1, 3.01) * mm});
            skLineSegment(sketch, "E992", {"start": v(-1, 3.01) * mm, "end": v(-1.05, 2.93) * mm});
            skLineSegment(sketch, "E993", {"start": v(-1.05, 2.93) * mm, "end": v(-1.1, 2.85) * mm});
            skLineSegment(sketch, "E994", {"start": v(-1.1, 2.85) * mm, "end": v(-1.15, 2.79) * mm});
            skLineSegment(sketch, "E995", {"start": v(-1.15, 2.79) * mm, "end": v(-1.2, 2.73) * mm});
            skLineSegment(sketch, "E996", {"start": v(-1.2, 2.73) * mm, "end": v(-1.26, 2.68) * mm});
            skLineSegment(sketch, "E997", {"start": v(-1.26, 2.68) * mm, "end": v(-1.4, 2.71) * mm});
            skLineSegment(sketch, "E998", {"start": v(-1.4, 2.71) * mm, "end": v(-1.55, 2.75) * mm});
            skLineSegment(sketch, "E999", {"start": v(-1.55, 2.75) * mm, "end": v(-1.6, 2.76) * mm});
            skLineSegment(sketch, "E1000", {"start": v(-1.6, 2.76) * mm, "end": v(-1.66, 2.79) * mm});
            skLineSegment(sketch, "E1001", {"start": v(-1.66, 2.79) * mm, "end": v(-1.7, 2.82) * mm});
            skLineSegment(sketch, "E1002", {"start": v(-1.7, 2.82) * mm, "end": v(-1.76, 2.86) * mm});
            skLineSegment(sketch, "E1003", {"start": v(-1.76, 2.86) * mm, "end": v(-1.8, 2.9) * mm});
            skLineSegment(sketch, "E1004", {"start": v(-1.8, 2.9) * mm, "end": v(-1.85, 2.94) * mm});
            skLineSegment(sketch, "E1005", {"start": v(-1.85, 2.94) * mm, "end": v(-1.94, 3.04) * mm});
            skLineSegment(sketch, "E1006", {"start": v(-1.94, 3.04) * mm, "end": v(-2.01, 3.14) * mm});
            skLineSegment(sketch, "E1007", {"start": v(-2.01, 3.14) * mm, "end": v(-2.08, 3.24) * mm});
            skLineSegment(sketch, "E1008", {"start": v(-2.08, 3.24) * mm, "end": v(-2.2, 3.4) * mm});
            skLineSegment(sketch, "E1009", {"start": v(-2.2, 3.4) * mm, "end": v(-2.13, 3.41) * mm});
            skLineSegment(sketch, "E1010", {"start": v(-2.13, 3.41) * mm, "end": v(-2.06, 3.43) * mm});
            skLineSegment(sketch, "E1011", {"start": v(-2.06, 3.43) * mm, "end": v(-2, 3.45) * mm});
            skLineSegment(sketch, "E1012", {"start": v(-2, 3.45) * mm, "end": v(-1.91, 3.48) * mm});
            skLineSegment(sketch, "E1013", {"start": v(-1.91, 3.48) * mm, "end": v(-1.83, 3.53) * mm});
            skLineSegment(sketch, "E1014", {"start": v(-1.83, 3.53) * mm, "end": v(-1.75, 3.59) * mm});
            skLineSegment(sketch, "E1015", {"start": v(-1.75, 3.59) * mm, "end": v(-1.65, 3.66) * mm});
            skLineSegment(sketch, "E1016", {"start": v(-1.65, 3.66) * mm, "end": v(-1.56, 3.74) * mm});
            skLineSegment(sketch, "E1017", {"start": v(-1.56, 3.74) * mm, "end": v(-1.7, 3.73) * mm});
            skLineSegment(sketch, "E1018", {"start": v(-1.7, 3.73) * mm, "end": v(-1.81, 3.72) * mm});
            skLineSegment(sketch, "E1019", {"start": v(-1.81, 3.72) * mm, "end": v(-1.92, 3.71) * mm});
            skLineSegment(sketch, "E1020", {"start": v(-1.92, 3.71) * mm, "end": v(-2.02, 3.72) * mm});
            skLineSegment(sketch, "E1021", {"start": v(-2.02, 3.72) * mm, "end": v(-2.1, 3.72) * mm});
            skLineSegment(sketch, "E1022", {"start": v(-2.1, 3.72) * mm, "end": v(-2.2, 3.74) * mm});
            skLineSegment(sketch, "E1023", {"start": v(-2.2, 3.74) * mm, "end": v(-2.27, 3.76) * mm});
            skLineSegment(sketch, "E1024", {"start": v(-2.27, 3.76) * mm, "end": v(-2.34, 3.8) * mm});
            skLineSegment(sketch, "E1025", {"start": v(-2.34, 3.8) * mm, "end": v(-2.35, 3.85) * mm});
            skLineSegment(sketch, "E1026", {"start": v(-2.35, 3.85) * mm, "end": v(-2.35, 3.9) * mm});
            skLineSegment(sketch, "E1027", {"start": v(-2.35, 3.9) * mm, "end": v(-2.35, 3.97) * mm});
            skLineSegment(sketch, "E1028", {"start": v(-2.35, 3.97) * mm, "end": v(-2.35, 4.03) * mm});
            skLineSegment(sketch, "E1029", {"start": v(-2.35, 4.03) * mm, "end": v(-2.34, 4.09) * mm});
            skLineSegment(sketch, "E1030", {"start": v(-2.34, 4.09) * mm, "end": v(-2.33, 4.15) * mm});
            skLineSegment(sketch, "E1031", {"start": v(-2.33, 4.15) * mm, "end": v(-2.32, 4.2) * mm});
            skLineSegment(sketch, "E1032", {"start": v(-2.32, 4.2) * mm, "end": v(-2.3, 4.26) * mm});
            skLineSegment(sketch, "E1033", {"start": v(-2.3, 4.26) * mm, "end": v(-2.29, 4.32) * mm});
            skLineSegment(sketch, "E1034", {"start": v(-2.29, 4.32) * mm, "end": v(-2.27, 4.38) * mm});
            skLineSegment(sketch, "E1035", {"start": v(-2.27, 4.38) * mm, "end": v(-2.24, 4.44) * mm});
            skLineSegment(sketch, "E1036", {"start": v(-2.24, 4.44) * mm, "end": v(-2.22, 4.5) * mm});
            skLineSegment(sketch, "E1037", {"start": v(-2.22, 4.5) * mm, "end": v(-2.19, 4.55) * mm});
            skLineSegment(sketch, "E1038", {"start": v(-2.19, 4.55) * mm, "end": v(-2.16, 4.6) * mm});
            skLineSegment(sketch, "E1039", {"start": v(-2.16, 4.6) * mm, "end": v(-2.12, 4.66) * mm});
            skLineSegment(sketch, "E1040", {"start": v(-2.12, 4.66) * mm, "end": v(-2.09, 4.7) * mm});
            skLineSegment(sketch, "E1041", {"start": v(-2.09, 4.7) * mm, "end": v(-2.05, 4.65) * mm});
            skLineSegment(sketch, "E1042", {"start": v(-2.05, 4.65) * mm, "end": v(-2, 4.6) * mm});
            skLineSegment(sketch, "E1043", {"start": v(-2, 4.6) * mm, "end": v(-1.96, 4.57) * mm});
            skLineSegment(sketch, "E1044", {"start": v(-1.96, 4.57) * mm, "end": v(-1.93, 4.54) * mm});
            skLineSegment(sketch, "E1045", {"start": v(-1.93, 4.54) * mm, "end": v(-1.9, 4.51) * mm});
            skLineSegment(sketch, "E1046", {"start": v(-1.9, 4.51) * mm, "end": v(-1.85, 4.49) * mm});
            skLineSegment(sketch, "E1047", {"start": v(-1.85, 4.49) * mm, "end": v(-1.8, 4.46) * mm});
            skLineSegment(sketch, "E1048", {"start": v(-1.8, 4.46) * mm, "end": v(-1.76, 4.44) * mm});
            skLineSegment(sketch, "E1049", {"start": v(-1.76, 4.44) * mm, "end": v(-1.7, 4.42) * mm});
            skLineSegment(sketch, "E1050", {"start": v(-1.7, 4.42) * mm, "end": v(-1.65, 4.4) * mm});
            skLineSegment(sketch, "E1051", {"start": v(-1.65, 4.4) * mm, "end": v(-1.58, 4.38) * mm});
            skLineSegment(sketch, "E1052", {"start": v(-1.58, 4.38) * mm, "end": v(-1.52, 4.36) * mm});
            skLineSegment(sketch, "E1053", {"start": v(-1.52, 4.36) * mm, "end": v(-1.44, 4.35) * mm});
            skLineSegment(sketch, "E1054", {"start": v(-1.44, 4.35) * mm, "end": v(-1.36, 4.33) * mm});
            skLineSegment(sketch, "E1055", {"start": v(-1.36, 4.33) * mm, "end": v(-1.46, 4.44) * mm});
            skLineSegment(sketch, "E1056", {"start": v(-1.46, 4.44) * mm, "end": v(-1.55, 4.53) * mm});
            skLineSegment(sketch, "E1057", {"start": v(-1.55, 4.53) * mm, "end": v(-1.63, 4.62) * mm});
            skLineSegment(sketch, "E1058", {"start": v(-1.63, 4.62) * mm, "end": v(-1.69, 4.7) * mm});
            skLineSegment(sketch, "E1059", {"start": v(-1.69, 4.7) * mm, "end": v(-1.74, 4.78) * mm});
            skLineSegment(sketch, "E1060", {"start": v(-1.74, 4.78) * mm, "end": v(-1.77, 4.86) * mm});
            skLineSegment(sketch, "E1061", {"start": v(-1.77, 4.86) * mm, "end": v(-1.8, 4.94) * mm});
            skLineSegment(sketch, "E1062", {"start": v(-1.8, 4.94) * mm, "end": v(-1.82, 5.03) * mm});
            skLineSegment(sketch, "E1063", {"start": v(-1.82, 5.03) * mm, "end": v(-1.72, 5.15) * mm});
            skLineSegment(sketch, "E1064", {"start": v(-1.72, 5.15) * mm, "end": v(-1.62, 5.28) * mm});
            skLineSegment(sketch, "E1065", {"start": v(-1.62, 5.28) * mm, "end": v(-1.53, 5.4) * mm});
            skLineSegment(sketch, "E1066", {"start": v(-1.53, 5.4) * mm, "end": v(-1.44, 5.53) * mm});
            skLineSegment(sketch, "E1067", {"start": v(-1.44, 5.53) * mm, "end": v(-1.39, 5.48) * mm});
            skLineSegment(sketch, "E1068", {"start": v(-1.39, 5.48) * mm, "end": v(-1.33, 5.44) * mm});
            skLineSegment(sketch, "E1069", {"start": v(-1.33, 5.44) * mm, "end": v(-1.26, 5.4) * mm});
            skLineSegment(sketch, "E1070", {"start": v(-1.26, 5.4) * mm, "end": v(-1.18, 5.38) * mm});
            skLineSegment(sketch, "E1071", {"start": v(-1.18, 5.38) * mm, "end": v(-1.08, 5.35) * mm});
            skLineSegment(sketch, "E1072", {"start": v(-1.08, 5.35) * mm, "end": v(-0.98, 5.33) * mm});
            skLineSegment(sketch, "E1073", {"start": v(-0.98, 5.33) * mm, "end": v(-0.86, 5.31) * mm});
            skLineSegment(sketch, "E1074", {"start": v(-0.86, 5.31) * mm, "end": v(-0.72, 5.3) * mm});
            skLineSegment(sketch, "E1075", {"start": v(-0.72, 5.3) * mm, "end": v(-0.82, 5.38) * mm});
            skLineSegment(sketch, "E1076", {"start": v(-0.82, 5.38) * mm, "end": v(-0.91, 5.46) * mm});
            skLineSegment(sketch, "E1077", {"start": v(-0.91, 5.46) * mm, "end": v(-0.99, 5.53) * mm});
            skLineSegment(sketch, "E1078", {"start": v(-0.99, 5.53) * mm, "end": v(-1.06, 5.6) * mm});
            skLineSegment(sketch, "E1079", {"start": v(-1.06, 5.6) * mm, "end": v(-1.11, 5.65) * mm});
            skLineSegment(sketch, "E1080", {"start": v(-1.11, 5.65) * mm, "end": v(-1.16, 5.72) * mm});
            skLineSegment(sketch, "E1081", {"start": v(-1.16, 5.72) * mm, "end": v(-1.2, 5.78) * mm});
            skLineSegment(sketch, "E1082", {"start": v(-1.2, 5.78) * mm, "end": v(-1.23, 5.85) * mm});
            skLineSegment(sketch, "E1083", {"start": v(-1.23, 5.85) * mm, "end": v(-1.15, 6) * mm});
            skLineSegment(sketch, "E1084", {"start": v(-1.15, 6) * mm, "end": v(-1.08, 6.15) * mm});
            skLineSegment(sketch, "E1085", {"start": v(-1.08, 6.15) * mm, "end": v(-1.05, 6.23) * mm});
            skLineSegment(sketch, "E1086", {"start": v(-1.05, 6.23) * mm, "end": v(-1.03, 6.3) * mm});
            skLineSegment(sketch, "E1087", {"start": v(-1.03, 6.3) * mm, "end": v(-1, 6.37) * mm});
            skLineSegment(sketch, "E1088", {"start": v(-1, 6.37) * mm, "end": v(-0.98, 6.45) * mm});
            skLineSegment(sketch, "E1089", {"start": v(-0.98, 6.45) * mm, "end": v(-0.96, 6.52) * mm});
            skLineSegment(sketch, "E1090", {"start": v(-0.96, 6.52) * mm, "end": v(-0.95, 6.6) * mm});
            skLineSegment(sketch, "E1091", {"start": v(-0.95, 6.6) * mm, "end": v(-0.94, 6.67) * mm});
            skLineSegment(sketch, "E1092", {"start": v(-0.94, 6.67) * mm, "end": v(-0.93, 6.74) * mm});
            skLineSegment(sketch, "E1093", {"start": v(-0.93, 6.74) * mm, "end": v(-0.93, 6.82) * mm});
            skLineSegment(sketch, "E1094", {"start": v(-0.93, 6.82) * mm, "end": v(-0.93, 6.9) * mm});
            skLineSegment(sketch, "E1095", {"start": v(-0.93, 6.9) * mm, "end": v(-0.93, 6.96) * mm});
            skLineSegment(sketch, "E1096", {"start": v(-0.93, 6.96) * mm, "end": v(-0.94, 7.03) * mm});
            skLineSegment(sketch, "E1097", {"start": v(-0.94, 7.03) * mm, "end": v(-0.88, 7.02) * mm});
            skLineSegment(sketch, "E1098", {"start": v(-0.88, 7.02) * mm, "end": v(-0.83, 7) * mm});
            skLineSegment(sketch, "E1099", {"start": v(-0.83, 7) * mm, "end": v(-0.77, 6.97) * mm});
            skLineSegment(sketch, "E1100", {"start": v(-0.77, 6.97) * mm, "end": v(-0.71, 6.95) * mm});
            skLineSegment(sketch, "E1101", {"start": v(-0.71, 6.95) * mm, "end": v(-0.65, 6.92) * mm});
            skLineSegment(sketch, "E1102", {"start": v(-0.65, 6.92) * mm, "end": v(-0.6, 6.88) * mm});
            skLineSegment(sketch, "E1103", {"start": v(-0.6, 6.88) * mm, "end": v(-0.54, 6.84) * mm});
            skLineSegment(sketch, "E1104", {"start": v(-0.54, 6.84) * mm, "end": v(-0.49, 6.8) * mm});
            skLineSegment(sketch, "E1105", {"start": v(-0.49, 6.8) * mm, "end": v(-0.43, 6.75) * mm});
            skLineSegment(sketch, "E1106", {"start": v(-0.43, 6.75) * mm, "end": v(-0.37, 6.7) * mm});
            skLineSegment(sketch, "E1107", {"start": v(-0.37, 6.7) * mm, "end": v(-0.32, 6.64) * mm});
            skLineSegment(sketch, "E1108", {"start": v(-0.32, 6.64) * mm, "end": v(-0.26, 6.57) * mm});
            skLineSegment(sketch, "E1109", {"start": v(-0.26, 6.57) * mm, "end": v(-0.2, 6.5) * mm});
            skLineSegment(sketch, "E1110", {"start": v(-0.2, 6.5) * mm, "end": v(-0.15, 6.43) * mm});
            skLineSegment(sketch, "E1111", {"start": v(-0.15, 6.43) * mm, "end": v(-0.09, 6.35) * mm});
            skLineSegment(sketch, "E1112", {"start": v(-0.09, 6.35) * mm, "end": v(-0.03, 6.27) * mm});
            skLineSegment(sketch, "E1113", {"start": v(-0.03, 6.27) * mm, "end": v(-0.08, 6.4) * mm});
            skLineSegment(sketch, "E1114", {"start": v(-0.08, 6.4) * mm, "end": v(-0.14, 6.51) * mm});
            skLineSegment(sketch, "E1115", {"start": v(-0.14, 6.51) * mm, "end": v(-0.2, 6.63) * mm});
            skLineSegment(sketch, "E1116", {"start": v(-0.2, 6.63) * mm, "end": v(-0.25, 6.74) * mm});
            skLineSegment(sketch, "E1117", {"start": v(-0.25, 6.74) * mm, "end": v(-0.31, 6.84) * mm});
            skLineSegment(sketch, "E1118", {"start": v(-0.31, 6.84) * mm, "end": v(-0.37, 6.94) * mm});
            skLineSegment(sketch, "E1119", {"start": v(-0.37, 6.94) * mm, "end": v(-0.43, 7.03) * mm});
            skLineSegment(sketch, "E1120", {"start": v(-0.43, 7.03) * mm, "end": v(-0.5, 7.12) * mm});
            skLineSegment(sketch, "E1121", {"start": v(-0.5, 7.12) * mm, "end": v(-0.57, 7.2) * mm});
            skLineSegment(sketch, "E1122", {"start": v(-0.57, 7.2) * mm, "end": v(-0.64, 7.28) * mm});
            skLineSegment(sketch, "E1123", {"start": v(-0.64, 7.28) * mm, "end": v(-0.7, 7.35) * mm});
            skLineSegment(sketch, "E1124", {"start": v(-0.7, 7.35) * mm, "end": v(-0.78, 7.42) * mm});
            skLineSegment(sketch, "E1125", {"start": v(-0.78, 7.42) * mm, "end": v(-0.86, 7.49) * mm});
            skLineSegment(sketch, "E1126", {"start": v(-0.86, 7.49) * mm, "end": v(-0.95, 7.55) * mm});
            skLineSegment(sketch, "E1127", {"start": v(-0.95, 7.55) * mm, "end": v(-1.03, 7.6) * mm});
            skLineSegment(sketch, "E1128", {"start": v(-1.03, 7.6) * mm, "end": v(-1.12, 7.65) * mm});
            skLineSegment(sketch, "E1129", {"start": v(-1.12, 7.65) * mm, "end": v(-1.05, 7.69) * mm});
            skLineSegment(sketch, "E1130", {"start": v(-1.05, 7.69) * mm, "end": v(-0.96, 7.71) * mm});
            skLineSegment(sketch, "E1131", {"start": v(-0.96, 7.71) * mm, "end": v(-0.87, 7.74) * mm});
            skLineSegment(sketch, "E1132", {"start": v(-0.87, 7.74) * mm, "end": v(-0.78, 7.76) * mm});
            skLineSegment(sketch, "E1133", {"start": v(-0.78, 7.76) * mm, "end": v(-0.69, 7.77) * mm});
            skLineSegment(sketch, "E1134", {"start": v(-0.69, 7.77) * mm, "end": v(-0.6, 7.78) * mm});
            skLineSegment(sketch, "E1135", {"start": v(-0.6, 7.78) * mm, "end": v(-0.5, 7.78) * mm});
            skLineSegment(sketch, "E1136", {"start": v(-0.5, 7.78) * mm, "end": v(-0.4, 7.78) * mm});
            skLineSegment(sketch, "E1137", {"start": v(-0.4, 7.78) * mm, "end": v(-0.29, 7.77) * mm});
            skLineSegment(sketch, "E1138", {"start": v(-0.29, 7.77) * mm, "end": v(-0.18, 7.76) * mm});
            skLineSegment(sketch, "E1139", {"start": v(-0.18, 7.76) * mm, "end": v(-0.08, 7.74) * mm});
            skLineSegment(sketch, "E1140", {"start": v(-0.08, 7.74) * mm, "end": v(0.03, 7.72) * mm});
            skLineSegment(sketch, "E1141", {"start": v(0.03, 7.72) * mm, "end": v(0.14, 7.69) * mm});
            skLineSegment(sketch, "E1142", {"start": v(0.14, 7.69) * mm, "end": v(0.24, 7.65) * mm});
            skLineSegment(sketch, "E1143", {"start": v(0.24, 7.65) * mm, "end": v(0.35, 7.6) * mm});
            skLineSegment(sketch, "E1144", {"start": v(0.35, 7.6) * mm, "end": v(0.46, 7.55) * mm});
            skLineSegment(sketch, "E1145", {"start": v(0.46, 7.55) * mm, "end": v(0.39, 7.64) * mm});
            skLineSegment(sketch, "E1146", {"start": v(0.39, 7.64) * mm, "end": v(0.3, 7.72) * mm});
            skLineSegment(sketch, "E1147", {"start": v(0.3, 7.72) * mm, "end": v(0.22, 7.79) * mm});
            skLineSegment(sketch, "E1148", {"start": v(0.22, 7.79) * mm, "end": v(0.13, 7.85) * mm});
            skLineSegment(sketch, "E1149", {"start": v(0.13, 7.85) * mm, "end": v(0.04, 7.9) * mm});
            skLineSegment(sketch, "E1150", {"start": v(0.04, 7.9) * mm, "end": v(-0.06, 7.96) * mm});
            skLineSegment(sketch, "E1151", {"start": v(-0.06, 7.96) * mm, "end": v(-0.16, 8) * mm});
            skLineSegment(sketch, "E1152", {"start": v(-0.16, 8) * mm, "end": v(-0.27, 8.03) * mm});
            skLineSegment(sketch, "E1153", {"start": v(-0.27, 8.03) * mm, "end": v(-0.38, 8.06) * mm});
            skLineSegment(sketch, "E1154", {"start": v(-0.38, 8.06) * mm, "end": v(-0.5, 8.08) * mm});
            skLineSegment(sketch, "E1155", {"start": v(-0.5, 8.08) * mm, "end": v(-0.61, 8.1) * mm});
            skLineSegment(sketch, "E1156", {"start": v(-0.61, 8.1) * mm, "end": v(-0.74, 8.1) * mm});
            skLineSegment(sketch, "E1157", {"start": v(-0.74, 8.1) * mm, "end": v(-0.87, 8.1) * mm});
            skLineSegment(sketch, "E1158", {"start": v(-0.87, 8.1) * mm, "end": v(-1, 8.1) * mm});
            skLineSegment(sketch, "E1159", {"start": v(-1, 8.1) * mm, "end": v(-1.14, 8.08) * mm});
            skLineSegment(sketch, "E1160", {"start": v(-1.14, 8.08) * mm, "end": v(-1.28, 8.06) * mm});
            skLineSegment(sketch, "E1161", {"start": v(-1.28, 8.06) * mm, "end": v(-1.23, 8.1) * mm});
            skLineSegment(sketch, "E1162", {"start": v(-1.23, 8.1) * mm, "end": v(-1.17, 8.15) * mm});
            skLineSegment(sketch, "E1163", {"start": v(-1.17, 8.15) * mm, "end": v(-1.1, 8.2) * mm});
            skLineSegment(sketch, "E1164", {"start": v(-1.1, 8.2) * mm, "end": v(-1.04, 8.24) * mm});
            skLineSegment(sketch, "E1165", {"start": v(-1.04, 8.24) * mm, "end": v(-0.95, 8.28) * mm});
            skLineSegment(sketch, "E1166", {"start": v(-0.95, 8.28) * mm, "end": v(-0.87, 8.32) * mm});
            skLineSegment(sketch, "E1167", {"start": v(-0.87, 8.32) * mm, "end": v(-0.77, 8.36) * mm});
            skLineSegment(sketch, "E1168", {"start": v(-0.77, 8.36) * mm, "end": v(-0.67, 8.4) * mm});
            skLineSegment(sketch, "E1169", {"start": v(-0.67, 8.4) * mm, "end": v(-0.56, 8.42) * mm});
            skLineSegment(sketch, "E1170", {"start": v(-0.56, 8.42) * mm, "end": v(-0.44, 8.44) * mm});
            skLineSegment(sketch, "E1171", {"start": v(-0.44, 8.44) * mm, "end": v(-0.31, 8.46) * mm});
            skLineSegment(sketch, "E1172", {"start": v(-0.31, 8.46) * mm, "end": v(-0.18, 8.47) * mm});
            skLineSegment(sketch, "E1173", {"start": v(-0.18, 8.47) * mm, "end": v(-0.04, 8.47) * mm});
            skLineSegment(sketch, "E1174", {"start": v(-0.04, 8.47) * mm, "end": v(0.1, 8.46) * mm});
            skLineSegment(sketch, "E1175", {"start": v(0.1, 8.46) * mm, "end": v(0.25, 8.45) * mm});
            skLineSegment(sketch, "E1176", {"start": v(0.25, 8.45) * mm, "end": v(0.4, 8.42) * mm});
            skLineSegment(sketch, "E1177", {"start": v(0.4, 8.42) * mm, "end": v(0.27, 8.47) * mm});
            skLineSegment(sketch, "E1178", {"start": v(0.27, 8.47) * mm, "end": v(0.13, 8.52) * mm});
            skLineSegment(sketch, "E1179", {"start": v(0.13, 8.52) * mm, "end": v(0, 8.55) * mm});
            skLineSegment(sketch, "E1180", {"start": v(0, 8.55) * mm, "end": v(-0.14, 8.58) * mm});
            skLineSegment(sketch, "E1181", {"start": v(-0.14, 8.58) * mm, "end": v(-0.27, 8.6) * mm});
            skLineSegment(sketch, "E1182", {"start": v(-0.27, 8.6) * mm, "end": v(-0.4, 8.6) * mm});
            skLineSegment(sketch, "E1183", {"start": v(-0.4, 8.6) * mm, "end": v(-0.53, 8.61) * mm});
            skLineSegment(sketch, "E1184", {"start": v(-0.53, 8.61) * mm, "end": v(-0.66, 8.6) * mm});
            skLineSegment(sketch, "E1185", {"start": v(-0.66, 8.6) * mm, "end": v(-0.78, 8.6) * mm});
            skLineSegment(sketch, "E1186", {"start": v(-0.78, 8.6) * mm, "end": v(-0.9, 8.58) * mm});
            skLineSegment(sketch, "E1187", {"start": v(-0.9, 8.58) * mm, "end": v(-1, 8.56) * mm});
            skLineSegment(sketch, "E1188", {"start": v(-1, 8.56) * mm, "end": v(-1.12, 8.53) * mm});
            skLineSegment(sketch, "E1189", {"start": v(-1.12, 8.53) * mm, "end": v(-1.22, 8.5) * mm});
            skLineSegment(sketch, "E1190", {"start": v(-1.22, 8.5) * mm, "end": v(-1.32, 8.46) * mm});
            skLineSegment(sketch, "E1191", {"start": v(-1.32, 8.46) * mm, "end": v(-1.41, 8.42) * mm});
            skLineSegment(sketch, "E1192", {"start": v(-1.41, 8.42) * mm, "end": v(-1.5, 8.37) * mm});
            skLineSegment(sketch, "E1193", {"start": v(-1.5, 8.37) * mm, "end": v(-1.5, 8.4) * mm});
            skLineSegment(sketch, "E1194", {"start": v(-1.5, 8.4) * mm, "end": v(-1.5, 8.43) * mm});
            skLineSegment(sketch, "E1195", {"start": v(-1.5, 8.43) * mm, "end": v(-1.5, 8.46) * mm});
            skLineSegment(sketch, "E1196", {"start": v(-1.5, 8.46) * mm, "end": v(-1.5, 8.5) * mm});
            skLineSegment(sketch, "E1197", {"start": v(-1.5, 8.5) * mm, "end": v(-1.49, 8.53) * mm});
            skLineSegment(sketch, "E1198", {"start": v(-1.49, 8.53) * mm, "end": v(-1.47, 8.58) * mm});
            skLineSegment(sketch, "E1199", {"start": v(-1.47, 8.58) * mm, "end": v(-1.45, 8.62) * mm});
            skLineSegment(sketch, "E1200", {"start": v(-1.45, 8.62) * mm, "end": v(-1.43, 8.66) * mm});
            skLineSegment(sketch, "E1201", {"start": v(-1.43, 8.66) * mm, "end": v(-1.4, 8.7) * mm});
            skLineSegment(sketch, "E1202", {"start": v(-1.4, 8.7) * mm, "end": v(-1.35, 8.75) * mm});
            skLineSegment(sketch, "E1203", {"start": v(-1.35, 8.75) * mm, "end": v(-1.3, 8.8) * mm});
            skLineSegment(sketch, "E1204", {"start": v(-1.3, 8.8) * mm, "end": v(-1.24, 8.84) * mm});
            skLineSegment(sketch, "E1205", {"start": v(-1.24, 8.84) * mm, "end": v(-1.17, 8.88) * mm});
            skLineSegment(sketch, "E1206", {"start": v(-1.17, 8.88) * mm, "end": v(-1.09, 8.91) * mm});
            skLineSegment(sketch, "E1207", {"start": v(-1.09, 8.91) * mm, "end": v(-1.02, 8.95) * mm});
            skLineSegment(sketch, "E1208", {"start": v(-1.02, 8.95) * mm, "end": v(-0.95, 8.99) * mm});
            skLineSegment(sketch, "E1209", {"start": v(-0.95, 8.99) * mm, "end": v(-0.88, 9.03) * mm});
            skLineSegment(sketch, "E1210", {"start": v(-0.88, 9.03) * mm, "end": v(-0.81, 9.09) * mm});
            skLineSegment(sketch, "E1211", {"start": v(-0.81, 9.09) * mm, "end": v(-0.75, 9.14) * mm});
            skLineSegment(sketch, "E1212", {"start": v(-0.75, 9.14) * mm, "end": v(-0.7, 9.2) * mm});
            skLineSegment(sketch, "E1213", {"start": v(-0.7, 9.2) * mm, "end": v(-0.64, 9.26) * mm});
            skLineSegment(sketch, "E1214", {"start": v(-0.64, 9.26) * mm, "end": v(-0.58, 9.32) * mm});
            skLineSegment(sketch, "E1215", {"start": v(-0.58, 9.32) * mm, "end": v(-0.5, 9.43) * mm});
            skLineSegment(sketch, "E1216", {"start": v(-0.5, 9.43) * mm, "end": v(-0.43, 9.52) * mm});
            skLineSegment(sketch, "E1217", {"start": v(-0.43, 9.52) * mm, "end": v(-0.37, 9.6) * mm});
            skSolve(sketch);
        }
        {
            var Q0;
            Q0 = qSketchRegion(id + "F3", true);
            extrude(context, id + "F4", {"entities" : qUnion([Q0]), "operationType" : NewBodyOperationType.REMOVE, "oppositeDirection" : true, "depth" : 25.4 * mm, "offsetDistance" : 25.4 * mm});
        }
        {
            var Q0;
            Q0=qCreatedBy(makeId("Top.planeOp"),FACE);
            var sketch = newSketch(context, id + "F5", { "sketchPlane" : qUnion([Q0])});
            skCircle(sketch, "E1218", {"center": v(0, 20.67) * mm, "radius": 3.94 * mm});
            skSolve(sketch);
        }
        {
            var Q0;
            Q0=makeQuery(id+"F5.imprint","IMPRINT",FACE,{"disambiguationData":[TD([[makeQuery(id+"F5.imprint","IMPRINT",EDGE,{"derivedFrom":sQuery(id+"F5.wireOp",EDGE,"E1218")}),1.0]])]});
            extrude(context, id + "F6", {"entities" : qUnion([Q0]), "operationType" : NewBodyOperationType.REMOVE, "depth" : 25.4 * mm, "offsetDistance" : 25.4 * mm});
        }
        {
            var Q0;
            Q0=makeQuery(id+"F6.boolean.opBoolean","INTERSECT",EDGE,{"derivedFrom":[makeQuery(id+"F1.opRevolve","SWEPT_FACE",FACE,{"disambiguationData":[OSD([sQuery(id+"F0.wireOp",EDGE,"E0")])]}),makeQuery(id+"F6.opExtrude","SWEPT_FACE",FACE,{"disambiguationData":[OSD([sQuery(id+"F5.wireOp",EDGE,"E1218")])]})]});
            fillet(context, id + "F7", {"entities" : qUnion([Q0]), "radius" : 1.52 * mm, "tangentPropagation" : true, "allowEdgeOverflow" : false});
        }
    });
